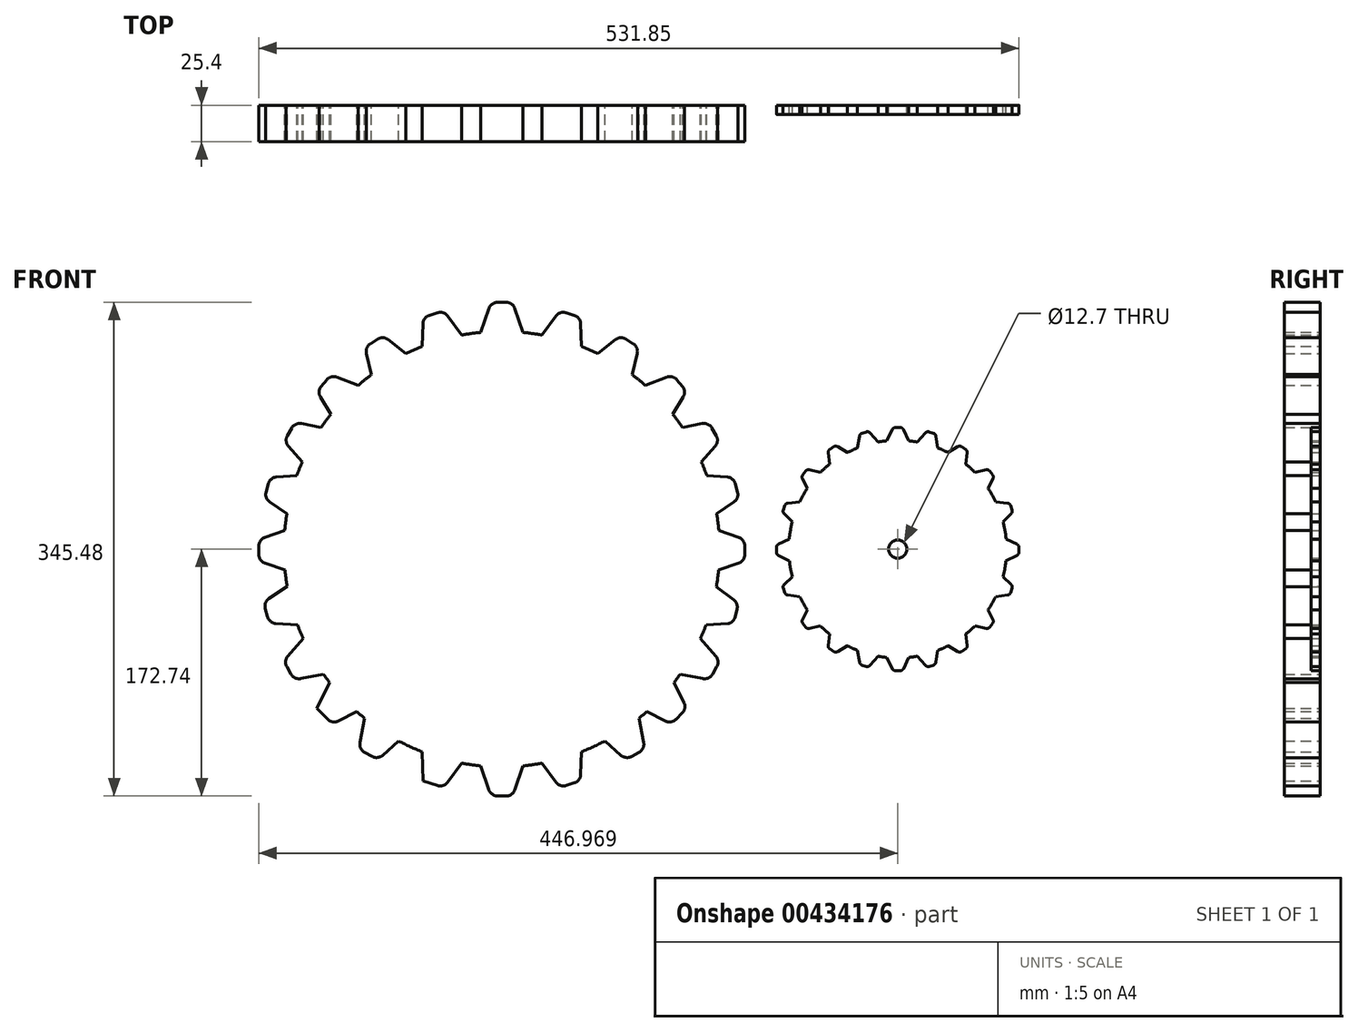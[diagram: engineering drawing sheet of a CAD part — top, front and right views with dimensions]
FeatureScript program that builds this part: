
annotation { "Feature Type Name" : "Feature", "Feature Type Description" : "" }
export const myFeature = defineFeature(function(context is Context, id is Id, definition is map)
    precondition{}
    {
        {
            var Q0;
            Q0=qCreatedBy(makeId("Front.planeOp"),FACE);
            var sketch = newSketch(context, id + "F0", { "sketchPlane" : qUnion([Q0])});
            skCircle(sketch, "E0", {"center": v(0, 0) * mm, "radius": 152.4 * mm});
            skCircle(sketch, "E1", {"center": v(0, 0) * mm, "radius": 6.35 * mm});
            skCircle(sketch, "E2", {"center": v(276.99, 0) * mm, "radius": 76.2 * mm});
            skCircle(sketch, "E3", {"center": v(276.99, 0) * mm, "radius": 6.35 * mm});
            skCircle(sketch, "E4.MirrorC", {"center": v(0, 0) * mm, "radius": 152.34 * mm});
            skLineSegment(sketch, "E5", {"start": v(3.18, 172.74) * mm, "end": v(-2.97, 172.74) * mm});
            skLineSegment(sketch, "E6", {"start": v(-8.98, 168.44) * mm, "end": v(-15.7, 148.7) * mm});
            skLineSegment(sketch, "E7", {"start": v(9.19, 168.44) * mm, "end": v(15.9, 148.7) * mm});
            skLineSegment(sketch, "E8", {"start": v(-15.7, 148.7) * mm, "end": v(15.9, 148.7) * mm});
            skLineSegment(sketch, "E9.MirrorCS", {"start": v(15.9, -148.7) * mm, "end": v(-15.7, -148.7) * mm});
            skLineSegment(sketch, "E10.MirrorCS", {"start": v(-8.98, -168.44) * mm, "end": v(-15.7, -148.7) * mm});
            skLineSegment(sketch, "E11.MirrorCS", {"start": v(9.19, -168.44) * mm, "end": v(15.9, -148.7) * mm});
            skLineSegment(sketch, "E12.MirrorCS", {"start": v(3.18, -172.74) * mm, "end": v(-2.97, -172.74) * mm});
            skLineSegment(sketch, "E13", {"start": v(-44.83, 165.44) * mm, "end": v(-50.7, 163.63) * mm});
            skLineSegment(sketch, "E14", {"start": v(-55.17, 157.74) * mm, "end": v(-55.75, 136.9) * mm});
            skLineSegment(sketch, "E15", {"start": v(-37.81, 163.1) * mm, "end": v(-25.57, 146.23) * mm});
            skLineSegment(sketch, "E16", {"start": v(-25.57, 146.23) * mm, "end": v(-55.75, 136.9) * mm});
            skLineSegment(sketch, "E17.0", {"start": v(-55.75, 136.9) * mm, "end": v(-25.57, 146.23) * mm, "construction": true});
            skLineSegment(sketch, "E18", {"start": v(-86.8, 146.99) * mm, "end": v(-92, 143.69) * mm});
            skLineSegment(sketch, "E19", {"start": v(-94.75, 136.83) * mm, "end": v(-89.8, 116.57) * mm});
            skLineSegment(sketch, "E20", {"start": v(-79.43, 146.59) * mm, "end": v(-63.16, 133.55) * mm});
            skLineSegment(sketch, "E21", {"start": v(-63.16, 133.55) * mm, "end": v(-89.8, 116.57) * mm});
            skLineSegment(sketch, "E22.0", {"start": v(-89.8, 116.57) * mm, "end": v(-63.16, 133.55) * mm, "construction": true});
            skLineSegment(sketch, "E23", {"start": v(-122.43, 118.55) * mm, "end": v(-126.38, 113.84) * mm});
            skLineSegment(sketch, "E24", {"start": v(-126.95, 106.47) * mm, "end": v(-116.14, 88.64) * mm});
            skLineSegment(sketch, "E25", {"start": v(-115.27, 120.39) * mm, "end": v(-95.83, 112.84) * mm});
            skLineSegment(sketch, "E26", {"start": v(-95.83, 112.84) * mm, "end": v(-116.14, 88.64) * mm});
            skLineSegment(sketch, "E27.0", {"start": v(-116.14, 88.64) * mm, "end": v(-95.83, 112.84) * mm, "construction": true});
            skLineSegment(sketch, "E28", {"start": v(-146.98, 84.77) * mm, "end": v(-150.05, 79.45) * mm});
            skLineSegment(sketch, "E29", {"start": v(-149.33, 72.1) * mm, "end": v(-135.58, 56.4) * mm});
            skLineSegment(sketch, "E30", {"start": v(-140.24, 87.83) * mm, "end": v(-119.79, 83.77) * mm});
            skLineSegment(sketch, "E31", {"start": v(-119.79, 83.77) * mm, "end": v(-135.58, 56.4) * mm});
            skLineSegment(sketch, "E32.0", {"start": v(-135.58, 56.4) * mm, "end": v(-119.79, 83.77) * mm, "construction": true});
            skLineSegment(sketch, "E33", {"start": v(-163.39, 45.78) * mm, "end": v(-164.98, 39.84) * mm});
            skLineSegment(sketch, "E34", {"start": v(-162.38, 32.92) * mm, "end": v(-145.04, 21.33) * mm});
            skLineSegment(sketch, "E35", {"start": v(-157.67, 50.47) * mm, "end": v(-136.87, 51.84) * mm});
            skLineSegment(sketch, "E36", {"start": v(-136.87, 51.84) * mm, "end": v(-145.04, 21.33) * mm});
            skLineSegment(sketch, "E37.0", {"start": v(-145.04, 21.33) * mm, "end": v(-136.87, 51.84) * mm, "construction": true});
            skLineSegment(sketch, "E38", {"start": v(-169.98, 2.28) * mm, "end": v(-169.98, -3.87) * mm});
            skLineSegment(sketch, "E39", {"start": v(-165.68, -9.88) * mm, "end": v(-145.94, -16.6) * mm});
            skLineSegment(sketch, "E40", {"start": v(-165.68, 8.29) * mm, "end": v(-145.94, 15) * mm});
            skLineSegment(sketch, "E41", {"start": v(-145.94, 15) * mm, "end": v(-145.94, -16.6) * mm});
            skLineSegment(sketch, "E42", {"start": v(-165.5, -41.42) * mm, "end": v(-163.9, -47.35) * mm});
            skLineSegment(sketch, "E43", {"start": v(-158.2, -52.05) * mm, "end": v(-137.39, -53.42) * mm});
            skLineSegment(sketch, "E44", {"start": v(-162.9, -34.5) * mm, "end": v(-145.56, -22.9) * mm});
            skLineSegment(sketch, "E45", {"start": v(-145.56, -22.9) * mm, "end": v(-137.39, -53.42) * mm});
            skLineSegment(sketch, "E46.0", {"start": v(-137.39, -53.42) * mm, "end": v(-145.56, -22.9) * mm, "construction": true});
            skLineSegment(sketch, "E47", {"start": v(-150.42, -82.21) * mm, "end": v(-147.35, -87.53) * mm});
            skLineSegment(sketch, "E48", {"start": v(-140.62, -90.59) * mm, "end": v(-120.16, -86.53) * mm});
            skLineSegment(sketch, "E49", {"start": v(-149.7, -74.85) * mm, "end": v(-135.96, -59.17) * mm});
            skLineSegment(sketch, "E50", {"start": v(-135.96, -59.17) * mm, "end": v(-120.16, -86.53) * mm});
            skLineSegment(sketch, "E51.0", {"start": v(-120.16, -86.53) * mm, "end": v(-135.96, -59.17) * mm, "construction": true});
            skLineSegment(sketch, "E52", {"start": v(-129.47, -111.53) * mm, "end": v(-121.91, -119.1) * mm});
            skLineSegment(sketch, "E53", {"start": v(-114.62, -120.3) * mm, "end": v(-95.91, -111.09) * mm});
            skLineSegment(sketch, "E54", {"start": v(-129.47, -111.53) * mm, "end": v(-118.25, -88.75) * mm});
            skLineSegment(sketch, "E55", {"start": v(-118.25, -88.75) * mm, "end": v(-95.91, -111.09) * mm});
            skLineSegment(sketch, "E56.0", {"start": v(-95.91, -111.09) * mm, "end": v(-118.25, -88.75) * mm, "construction": true});
            skLineSegment(sketch, "E57", {"start": v(-96.16, -142.05) * mm, "end": v(-90.81, -145.08) * mm});
            skLineSegment(sketch, "E58", {"start": v(-83.46, -144.3) * mm, "end": v(-67.9, -130.42) * mm});
            skLineSegment(sketch, "E59", {"start": v(-99.27, -135.35) * mm, "end": v(-95.39, -114.86) * mm});
            skLineSegment(sketch, "E60", {"start": v(-95.39, -114.86) * mm, "end": v(-67.9, -130.42) * mm});
            skLineSegment(sketch, "E61.0", {"start": v(-67.9, -130.42) * mm, "end": v(-95.39, -114.86) * mm, "construction": true});
            skLineSegment(sketch, "E62.MirrorCS", {"start": v(-37.81, -163.1) * mm, "end": v(-25.57, -146.23) * mm});
            skLineSegment(sketch, "E63.MirrorCS", {"start": v(-55.75, -136.9) * mm, "end": v(-25.57, -146.23) * mm, "construction": true});
            skLineSegment(sketch, "E64.MirrorCS", {"start": v(-55.05, -162.29) * mm, "end": v(-55.75, -136.9) * mm});
            skLineSegment(sketch, "E65.MirrorCS", {"start": v(-44.83, -165.44) * mm, "end": v(-55.05, -162.29) * mm});
            skLineSegment(sketch, "E66.MirrorCS", {"start": v(157.67, 50.47) * mm, "end": v(136.87, 51.84) * mm});
            skLineSegment(sketch, "E67.MirrorCS", {"start": v(162.38, 32.92) * mm, "end": v(145.04, 21.33) * mm});
            skLineSegment(sketch, "E68.MirrorCS", {"start": v(163.39, 45.78) * mm, "end": v(164.98, 39.84) * mm});
            skLineSegment(sketch, "E69.MirrorCS", {"start": v(145.04, 21.33) * mm, "end": v(136.87, 51.84) * mm, "construction": true});
            skLineSegment(sketch, "E70.MirrorCS", {"start": v(145.94, 15) * mm, "end": v(145.94, -16.6) * mm});
            skLineSegment(sketch, "E71.MirrorCS", {"start": v(165.68, 8.29) * mm, "end": v(145.94, 15) * mm});
            skLineSegment(sketch, "E72.MirrorCS", {"start": v(169.98, 2.28) * mm, "end": v(169.98, -3.87) * mm});
            skLineSegment(sketch, "E73.MirrorCS", {"start": v(165.68, -9.88) * mm, "end": v(145.94, -16.6) * mm});
            skLineSegment(sketch, "E74.MirrorCS", {"start": v(137.39, -53.42) * mm, "end": v(145.56, -22.9) * mm, "construction": true});
            skLineSegment(sketch, "E75.MirrorCS", {"start": v(162.27, -35.45) * mm, "end": v(145.56, -22.9) * mm});
            skLineSegment(sketch, "E76.MirrorCS", {"start": v(164.59, -42.17) * mm, "end": v(163, -48.1) * mm});
            skLineSegment(sketch, "E77.MirrorCS", {"start": v(149.7, -74.85) * mm, "end": v(135.96, -59.17) * mm});
            skLineSegment(sketch, "E78.MirrorCS", {"start": v(150.42, -82.21) * mm, "end": v(147.35, -87.53) * mm});
            skLineSegment(sketch, "E79.MirrorCS", {"start": v(140.62, -90.59) * mm, "end": v(120.16, -86.53) * mm});
            skLineSegment(sketch, "E80.MirrorCS", {"start": v(120.16, -86.53) * mm, "end": v(135.96, -59.17) * mm, "construction": true});
            skLineSegment(sketch, "E81.MirrorCS", {"start": v(95.91, -111.09) * mm, "end": v(118.25, -88.75) * mm, "construction": true});
            skLineSegment(sketch, "E82.MirrorCS", {"start": v(114.62, -120.3) * mm, "end": v(95.91, -111.09) * mm});
            skLineSegment(sketch, "E83.MirrorCS", {"start": v(126.26, -114.75) * mm, "end": v(121.91, -119.1) * mm});
            skLineSegment(sketch, "E84.MirrorCS", {"start": v(127.46, -107.45) * mm, "end": v(118.25, -88.75) * mm});
            skLineSegment(sketch, "E85.MirrorCS", {"start": v(99.27, -135.35) * mm, "end": v(95.39, -114.86) * mm});
            skLineSegment(sketch, "E86.MirrorCS", {"start": v(67.9, -130.42) * mm, "end": v(95.39, -114.86) * mm, "construction": true});
            skLineSegment(sketch, "E87.MirrorCS", {"start": v(83.46, -144.3) * mm, "end": v(67.9, -130.42) * mm});
            skLineSegment(sketch, "E88.MirrorCS", {"start": v(96.16, -142.05) * mm, "end": v(90.81, -145.08) * mm});
            skLineSegment(sketch, "E89.MirrorCS", {"start": v(55.17, -157.74) * mm, "end": v(55.75, -136.9) * mm});
            skLineSegment(sketch, "E90.MirrorCS", {"start": v(55.75, -136.9) * mm, "end": v(25.57, -146.23) * mm, "construction": true});
            skLineSegment(sketch, "E91.MirrorCS", {"start": v(44.83, -165.44) * mm, "end": v(50.7, -163.63) * mm});
            skLineSegment(sketch, "E92.MirrorCS", {"start": v(37.81, -163.1) * mm, "end": v(25.57, -146.23) * mm});
            skLineSegment(sketch, "E93.MirrorCS", {"start": v(37.81, 163.1) * mm, "end": v(25.57, 146.23) * mm});
            skLineSegment(sketch, "E94.MirrorCS", {"start": v(55.17, 157.74) * mm, "end": v(55.75, 136.9) * mm});
            skLineSegment(sketch, "E95.MirrorCS", {"start": v(44.83, 165.44) * mm, "end": v(50.7, 163.63) * mm});
            skLineSegment(sketch, "E96.MirrorCS", {"start": v(55.75, 136.9) * mm, "end": v(25.57, 146.23) * mm, "construction": true});
            skLineSegment(sketch, "E97.MirrorCS", {"start": v(89.8, 116.57) * mm, "end": v(63.16, 133.55) * mm, "construction": true});
            skLineSegment(sketch, "E98.MirrorCS", {"start": v(79.43, 146.59) * mm, "end": v(63.16, 133.55) * mm});
            skLineSegment(sketch, "E99.MirrorCS", {"start": v(94.75, 136.83) * mm, "end": v(89.8, 116.57) * mm});
            skLineSegment(sketch, "E100.MirrorCS", {"start": v(86.8, 146.99) * mm, "end": v(92, 143.69) * mm});
            skLineSegment(sketch, "E101.MirrorCS", {"start": v(115.27, 120.39) * mm, "end": v(95.83, 112.84) * mm});
            skLineSegment(sketch, "E102.MirrorCS", {"start": v(122.43, 118.55) * mm, "end": v(126.38, 113.84) * mm});
            skLineSegment(sketch, "E103.MirrorCS", {"start": v(126.95, 106.47) * mm, "end": v(116.14, 88.64) * mm});
            skLineSegment(sketch, "E104.MirrorCS", {"start": v(116.14, 88.64) * mm, "end": v(95.83, 112.84) * mm, "construction": true});
            skLineSegment(sketch, "E105.MirrorCS", {"start": v(140.24, 87.83) * mm, "end": v(119.79, 83.77) * mm});
            skLineSegment(sketch, "E106.MirrorCS", {"start": v(146.98, 84.77) * mm, "end": v(150.05, 79.45) * mm});
            skLineSegment(sketch, "E107.MirrorCS", {"start": v(149.33, 72.1) * mm, "end": v(135.58, 56.4) * mm});
            skLineSegment(sketch, "E108.MirrorCS", {"start": v(135.58, 56.4) * mm, "end": v(119.79, 83.77) * mm, "construction": true});
            skLineSegment(sketch, "E109", {"start": v(193.5, -4.35) * mm, "end": v(203.46, -9.32) * mm});
            skLineSegment(sketch, "E110", {"start": v(192.1, -2.08) * mm, "end": v(192.1, 1.1) * mm});
            skLineSegment(sketch, "E111", {"start": v(193.56, 3.4) * mm, "end": v(203.6, 8.1) * mm});
            skLineSegment(sketch, "E112", {"start": v(203.6, 8.1) * mm, "end": v(203.46, -9.32) * mm});
            skLineSegment(sketch, "E113", {"start": v(250.25, 79.12) * mm, "end": v(248.45, 68.13) * mm});
            skLineSegment(sketch, "E114", {"start": v(252, 81.13) * mm, "end": v(255.03, 82.07) * mm});
            skLineSegment(sketch, "E115", {"start": v(257.66, 81.36) * mm, "end": v(265.14, 73.17) * mm});
            skLineSegment(sketch, "E116", {"start": v(265.14, 73.17) * mm, "end": v(248.45, 68.13) * mm});
            skLineSegment(sketch, "E117", {"start": v(228.41, 67.51) * mm, "end": v(229.64, 56.45) * mm});
            skLineSegment(sketch, "E118", {"start": v(229.56, 69.92) * mm, "end": v(232.22, 71.64) * mm});
            skLineSegment(sketch, "E119", {"start": v(234.94, 71.66) * mm, "end": v(244.35, 65.8) * mm});
            skLineSegment(sketch, "E120", {"start": v(244.35, 65.8) * mm, "end": v(229.64, 56.45) * mm});
            skLineSegment(sketch, "E121", {"start": v(210.32, 49.36) * mm, "end": v(215.2, 39.35) * mm});
            skLineSegment(sketch, "E122", {"start": v(210.59, 52.02) * mm, "end": v(212.51, 54.53) * mm});
            skLineSegment(sketch, "E123", {"start": v(215.07, 55.47) * mm, "end": v(225.9, 53.11) * mm});
            skLineSegment(sketch, "E124", {"start": v(225.9, 53.11) * mm, "end": v(215.2, 39.35) * mm});
            skLineSegment(sketch, "E125", {"start": v(197.57, 24.8) * mm, "end": v(205.5, 17) * mm});
            skLineSegment(sketch, "E126", {"start": v(196.94, 27.39) * mm, "end": v(197.91, 30.4) * mm});
            skLineSegment(sketch, "E127", {"start": v(200.01, 32.14) * mm, "end": v(211.01, 33.53) * mm});
            skLineSegment(sketch, "E128", {"start": v(211.01, 33.53) * mm, "end": v(205.5, 17) * mm});
            skLineSegment(sketch, "E129.MirrorCS", {"start": v(197.57, -24.8) * mm, "end": v(205.5, -17) * mm});
            skLineSegment(sketch, "E130.MirrorCS", {"start": v(211.01, -33.53) * mm, "end": v(205.5, -17) * mm});
            skLineSegment(sketch, "E131.MirrorCS", {"start": v(200.01, -32.14) * mm, "end": v(211.01, -33.53) * mm});
            skLineSegment(sketch, "E132.MirrorCS", {"start": v(196.94, -27.39) * mm, "end": v(197.91, -30.4) * mm});
            skLineSegment(sketch, "E133.MirrorCS", {"start": v(210.32, -49.36) * mm, "end": v(215.2, -39.35) * mm});
            skLineSegment(sketch, "E134.MirrorCS", {"start": v(225.9, -53.11) * mm, "end": v(215.2, -39.35) * mm});
            skLineSegment(sketch, "E135.MirrorCS", {"start": v(215.07, -55.47) * mm, "end": v(225.9, -53.11) * mm});
            skLineSegment(sketch, "E136.MirrorCS", {"start": v(210.59, -52.02) * mm, "end": v(212.51, -54.53) * mm});
            skLineSegment(sketch, "E137.MirrorCS", {"start": v(229.56, -69.92) * mm, "end": v(232.22, -71.64) * mm});
            skLineSegment(sketch, "E138.MirrorCS", {"start": v(228.41, -67.51) * mm, "end": v(229.64, -56.45) * mm});
            skLineSegment(sketch, "E139.MirrorCS", {"start": v(234.94, -71.66) * mm, "end": v(244.35, -65.8) * mm});
            skLineSegment(sketch, "E140.MirrorCS", {"start": v(244.35, -65.8) * mm, "end": v(229.64, -56.45) * mm});
            skLineSegment(sketch, "E141.MirrorCS", {"start": v(265.14, -73.17) * mm, "end": v(248.45, -68.13) * mm});
            skLineSegment(sketch, "E142.MirrorCS", {"start": v(250.25, -79.12) * mm, "end": v(248.45, -68.13) * mm});
            skLineSegment(sketch, "E143.MirrorCS", {"start": v(252, -81.13) * mm, "end": v(255.03, -82.07) * mm});
            skLineSegment(sketch, "E144.MirrorCS", {"start": v(257.66, -81.36) * mm, "end": v(265.14, -73.17) * mm});
            skLineSegment(sketch, "E145.MirrorCS", {"start": v(296.32, 81.36) * mm, "end": v(288.84, 73.17) * mm});
            skLineSegment(sketch, "E146.MirrorCS", {"start": v(288.84, 73.17) * mm, "end": v(305.53, 68.13) * mm});
            skLineSegment(sketch, "E147.MirrorCS", {"start": v(303.73, 79.12) * mm, "end": v(305.53, 68.13) * mm});
            skLineSegment(sketch, "E148.MirrorCS", {"start": v(301.97, 81.13) * mm, "end": v(298.95, 82.07) * mm});
            skLineSegment(sketch, "E149.MirrorCS", {"start": v(324.42, 69.92) * mm, "end": v(321.76, 71.64) * mm});
            skLineSegment(sketch, "E150.MirrorCS", {"start": v(319.04, 71.66) * mm, "end": v(309.63, 65.8) * mm});
            skLineSegment(sketch, "E151.MirrorCS", {"start": v(325.57, 67.51) * mm, "end": v(324.34, 56.45) * mm});
            skLineSegment(sketch, "E152.MirrorCS", {"start": v(309.63, 65.8) * mm, "end": v(324.34, 56.45) * mm});
            skLineSegment(sketch, "E153.MirrorCS", {"start": v(328.07, 53.11) * mm, "end": v(338.78, 39.35) * mm});
            skLineSegment(sketch, "E154.MirrorCS", {"start": v(338.9, 55.47) * mm, "end": v(328.07, 53.11) * mm});
            skLineSegment(sketch, "E155.MirrorCS", {"start": v(343.39, 52.02) * mm, "end": v(341.46, 54.53) * mm});
            skLineSegment(sketch, "E156.MirrorCS", {"start": v(343.66, 49.36) * mm, "end": v(338.78, 39.35) * mm});
            skLineSegment(sketch, "E157.MirrorCS", {"start": v(353.97, 32.14) * mm, "end": v(342.97, 33.53) * mm});
            skLineSegment(sketch, "E158.MirrorCS", {"start": v(342.97, 33.53) * mm, "end": v(348.47, 17) * mm});
            skLineSegment(sketch, "E159.MirrorCS", {"start": v(356.4, 24.8) * mm, "end": v(348.47, 17) * mm});
            skLineSegment(sketch, "E160.MirrorCS", {"start": v(357.04, 27.39) * mm, "end": v(356.06, 30.4) * mm});
            skLineSegment(sketch, "E161.MirrorCS", {"start": v(350.38, 8.1) * mm, "end": v(350.51, -9.32) * mm});
            skLineSegment(sketch, "E162.MirrorCS", {"start": v(360.41, 3.4) * mm, "end": v(350.38, 8.1) * mm});
            skLineSegment(sketch, "E163.MirrorCS", {"start": v(361.87, -2.08) * mm, "end": v(361.87, 1.1) * mm});
            skLineSegment(sketch, "E164.MirrorCS", {"start": v(360.47, -4.35) * mm, "end": v(350.51, -9.32) * mm});
            skLineSegment(sketch, "E165.MirrorCS", {"start": v(356.4, -24.8) * mm, "end": v(348.47, -17) * mm});
            skLineSegment(sketch, "E166.MirrorCS", {"start": v(357.04, -27.39) * mm, "end": v(356.06, -30.4) * mm});
            skLineSegment(sketch, "E167.MirrorCS", {"start": v(353.97, -32.14) * mm, "end": v(342.97, -33.53) * mm});
            skLineSegment(sketch, "E168.MirrorCS", {"start": v(342.97, -33.53) * mm, "end": v(348.47, -17) * mm});
            skLineSegment(sketch, "E169.MirrorCS", {"start": v(328.07, -53.11) * mm, "end": v(338.78, -39.35) * mm});
            skLineSegment(sketch, "E170.MirrorCS", {"start": v(343.66, -49.36) * mm, "end": v(338.78, -39.35) * mm});
            skLineSegment(sketch, "E171.MirrorCS", {"start": v(343.39, -52.02) * mm, "end": v(341.46, -54.53) * mm});
            skLineSegment(sketch, "E172.MirrorCS", {"start": v(338.9, -55.47) * mm, "end": v(328.07, -53.11) * mm});
            skLineSegment(sketch, "E173.MirrorCS", {"start": v(325.57, -67.51) * mm, "end": v(324.34, -56.45) * mm});
            skLineSegment(sketch, "E174.MirrorCS", {"start": v(309.63, -65.8) * mm, "end": v(324.34, -56.45) * mm});
            skLineSegment(sketch, "E175.MirrorCS", {"start": v(319.04, -71.66) * mm, "end": v(309.63, -65.8) * mm});
            skLineSegment(sketch, "E176.MirrorCS", {"start": v(324.42, -69.92) * mm, "end": v(321.76, -71.64) * mm});
            skLineSegment(sketch, "E177.MirrorCS", {"start": v(288.84, -73.17) * mm, "end": v(305.53, -68.13) * mm});
            skLineSegment(sketch, "E178.MirrorCS", {"start": v(303.73, -79.12) * mm, "end": v(305.53, -68.13) * mm});
            skLineSegment(sketch, "E179.MirrorCS", {"start": v(301.97, -81.13) * mm, "end": v(298.95, -82.07) * mm});
            skLineSegment(sketch, "E180.MirrorCS", {"start": v(296.32, -81.36) * mm, "end": v(288.84, -73.17) * mm});
            skLineSegment(sketch, "E181", {"start": v(273.24, 83.72) * mm, "end": v(268.26, 73.77) * mm});
            skLineSegment(sketch, "E182", {"start": v(275.51, 85.12) * mm, "end": v(278.68, 85.12) * mm});
            skLineSegment(sketch, "E183", {"start": v(280.98, 83.67) * mm, "end": v(285.7, 73.63) * mm});
            skLineSegment(sketch, "E184", {"start": v(285.7, 73.63) * mm, "end": v(268.26, 73.77) * mm});
            skLineSegment(sketch, "E185.MirrorCS", {"start": v(285.7, -73.63) * mm, "end": v(268.26, -73.77) * mm});
            skLineSegment(sketch, "E186.MirrorCS", {"start": v(280.98, -83.67) * mm, "end": v(285.7, -73.63) * mm});
            skLineSegment(sketch, "E187.MirrorCS", {"start": v(273.24, -83.72) * mm, "end": v(268.26, -73.77) * mm});
            skLineSegment(sketch, "E188.MirrorCS", {"start": v(275.51, -85.12) * mm, "end": v(278.68, -85.12) * mm});
            skPoint(sketch, "E189.visualSharp", {"position": v(-55.05, 162.29) * mm});
            skArc(sketch, "E189.filletArc", {"start": v(-50.7, 163.63) * mm, "mid": v(-53.88, 161.4) * mm, "end": v(-55.17, 157.74) * mm});
            skPoint(sketch, "E190.visualSharp", {"position": v(-40.49, 166.79) * mm});
            skArc(sketch, "E190.filletArc", {"start": v(-37.81, 163.1) * mm, "mid": v(-40.95, 165.4) * mm, "end": v(-44.83, 165.44) * mm});
            skPoint(sketch, "E191.visualSharp", {"position": v(-7.51, 172.74) * mm});
            skArc(sketch, "E191.filletArc", {"start": v(-2.97, 172.74) * mm, "mid": v(-6.66, 171.56) * mm, "end": v(-8.98, 168.44) * mm});
            skPoint(sketch, "E192.visualSharp", {"position": v(7.73, 172.74) * mm});
            skArc(sketch, "E192.filletArc", {"start": v(9.19, 168.44) * mm, "mid": v(6.88, 171.56) * mm, "end": v(3.18, 172.74) * mm});
            skPoint(sketch, "E193.visualSharp", {"position": v(40.49, 166.79) * mm});
            skArc(sketch, "E193.filletArc", {"start": v(44.83, 165.44) * mm, "mid": v(40.95, 165.4) * mm, "end": v(37.81, 163.1) * mm});
            skPoint(sketch, "E194.visualSharp", {"position": v(55.05, 162.29) * mm});
            skArc(sketch, "E194.filletArc", {"start": v(55.17, 157.74) * mm, "mid": v(53.88, 161.4) * mm, "end": v(50.7, 163.63) * mm});
            skPoint(sketch, "E195.visualSharp", {"position": v(82.97, 149.43) * mm});
            skArc(sketch, "E195.filletArc", {"start": v(86.8, 146.99) * mm, "mid": v(83.05, 147.98) * mm, "end": v(79.43, 146.59) * mm});
            skPoint(sketch, "E196.visualSharp", {"position": v(95.83, 141.24) * mm});
            skArc(sketch, "E196.filletArc", {"start": v(94.75, 136.83) * mm, "mid": v(94.47, 140.7) * mm, "end": v(92, 143.69) * mm});
            skPoint(sketch, "E197.visualSharp", {"position": v(119.5, 122.03) * mm});
            skArc(sketch, "E197.filletArc", {"start": v(122.43, 118.55) * mm, "mid": v(119.14, 120.62) * mm, "end": v(115.27, 120.39) * mm});
            skPoint(sketch, "E198.visualSharp", {"position": v(129.3, 110.36) * mm});
            skArc(sketch, "E198.filletArc", {"start": v(126.95, 106.47) * mm, "mid": v(127.85, 110.25) * mm, "end": v(126.38, 113.84) * mm});
            skPoint(sketch, "E199.visualSharp", {"position": v(144.7, 88.71) * mm});
            skArc(sketch, "E199.filletArc", {"start": v(146.98, 84.77) * mm, "mid": v(144.1, 87.38) * mm, "end": v(140.24, 87.83) * mm});
            skPoint(sketch, "E200.visualSharp", {"position": v(162.21, 50.17) * mm});
            skArc(sketch, "E200.filletArc", {"start": v(163.39, 45.78) * mm, "mid": v(161.29, 49.04) * mm, "end": v(157.67, 50.47) * mm});
            skPoint(sketch, "E201.visualSharp", {"position": v(166.16, 35.45) * mm});
            skArc(sketch, "E201.filletArc", {"start": v(162.38, 32.92) * mm, "mid": v(164.79, 35.96) * mm, "end": v(164.98, 39.84) * mm});
            skPoint(sketch, "E202.visualSharp", {"position": v(169.98, 6.82) * mm});
            skArc(sketch, "E202.filletArc", {"start": v(169.98, 2.28) * mm, "mid": v(168.8, 5.97) * mm, "end": v(165.68, 8.29) * mm});
            skPoint(sketch, "E203.visualSharp", {"position": v(169.98, -8.42) * mm});
            skArc(sketch, "E203.filletArc", {"start": v(165.68, -9.88) * mm, "mid": v(168.8, -7.57) * mm, "end": v(169.98, -3.87) * mm});
            skPoint(sketch, "E204.visualSharp", {"position": v(165.7, -38.03) * mm});
            skArc(sketch, "E204.filletArc", {"start": v(164.59, -42.17) * mm, "mid": v(164.45, -38.46) * mm, "end": v(162.27, -35.45) * mm});
            skPoint(sketch, "E205.visualSharp", {"position": v(152.7, -78.28) * mm});
            skArc(sketch, "E205.filletArc", {"start": v(150.42, -82.21) * mm, "mid": v(151.24, -78.42) * mm, "end": v(149.7, -74.85) * mm});
            skPoint(sketch, "E206.visualSharp", {"position": v(145.08, -91.47) * mm});
            skArc(sketch, "E206.filletArc", {"start": v(140.62, -90.59) * mm, "mid": v(144.47, -90.14) * mm, "end": v(147.35, -87.53) * mm});
            skPoint(sketch, "E207.visualSharp", {"position": v(129.47, -111.53) * mm});
            skArc(sketch, "E207.filletArc", {"start": v(126.26, -114.75) * mm, "mid": v(128.03, -111.3) * mm, "end": v(127.46, -107.45) * mm});
            skPoint(sketch, "E208.visualSharp", {"position": v(118.7, -122.3) * mm});
            skArc(sketch, "E208.filletArc", {"start": v(114.62, -120.3) * mm, "mid": v(118.46, -120.87) * mm, "end": v(121.91, -119.1) * mm});
            skPoint(sketch, "E209.visualSharp", {"position": v(100.12, -139.81) * mm});
            skArc(sketch, "E209.filletArc", {"start": v(96.16, -142.05) * mm, "mid": v(98.8, -139.2) * mm, "end": v(99.27, -135.35) * mm});
            skPoint(sketch, "E210.visualSharp", {"position": v(86.85, -147.32) * mm});
            skArc(sketch, "E210.filletArc", {"start": v(83.46, -144.3) * mm, "mid": v(87, -145.87) * mm, "end": v(90.81, -145.08) * mm});
            skPoint(sketch, "E211.visualSharp", {"position": v(55.05, -162.29) * mm});
            skArc(sketch, "E211.filletArc", {"start": v(50.7, -163.63) * mm, "mid": v(53.88, -161.4) * mm, "end": v(55.17, -157.74) * mm});
            skPoint(sketch, "E212.visualSharp", {"position": v(7.73, -172.74) * mm});
            skArc(sketch, "E212.filletArc", {"start": v(3.18, -172.74) * mm, "mid": v(6.88, -171.56) * mm, "end": v(9.19, -168.44) * mm});
            skPoint(sketch, "E213.visualSharp", {"position": v(40.49, -166.79) * mm});
            skArc(sketch, "E213.filletArc", {"start": v(37.81, -163.1) * mm, "mid": v(40.95, -165.4) * mm, "end": v(44.83, -165.44) * mm});
            skPoint(sketch, "E214.visualSharp", {"position": v(-7.51, -172.74) * mm});
            skArc(sketch, "E214.filletArc", {"start": v(-8.98, -168.44) * mm, "mid": v(-6.66, -171.56) * mm, "end": v(-2.97, -172.74) * mm});
            skPoint(sketch, "E215.visualSharp", {"position": v(-40.49, -166.79) * mm});
            skArc(sketch, "E215.filletArc", {"start": v(-44.83, -165.44) * mm, "mid": v(-40.95, -165.4) * mm, "end": v(-37.81, -163.1) * mm});
            skPoint(sketch, "E216.visualSharp", {"position": v(-86.85, -147.32) * mm});
            skArc(sketch, "E216.filletArc", {"start": v(-90.81, -145.08) * mm, "mid": v(-87, -145.87) * mm, "end": v(-83.46, -144.3) * mm});
            skPoint(sketch, "E217.visualSharp", {"position": v(-100.12, -139.81) * mm});
            skArc(sketch, "E217.filletArc", {"start": v(-99.27, -135.35) * mm, "mid": v(-98.8, -139.2) * mm, "end": v(-96.16, -142.05) * mm});
            skPoint(sketch, "E218.visualSharp", {"position": v(-118.7, -122.3) * mm});
            skArc(sketch, "E218.filletArc", {"start": v(-121.91, -119.1) * mm, "mid": v(-118.46, -120.87) * mm, "end": v(-114.62, -120.3) * mm});
            skPoint(sketch, "E219.visualSharp", {"position": v(-145.08, -91.47) * mm});
            skArc(sketch, "E219.filletArc", {"start": v(-147.35, -87.53) * mm, "mid": v(-144.47, -90.14) * mm, "end": v(-140.62, -90.59) * mm});
            skPoint(sketch, "E220.visualSharp", {"position": v(-152.7, -78.28) * mm});
            skArc(sketch, "E220.filletArc", {"start": v(-149.7, -74.85) * mm, "mid": v(-151.24, -78.42) * mm, "end": v(-150.42, -82.21) * mm});
            skPoint(sketch, "E221.visualSharp", {"position": v(-162.73, -51.75) * mm});
            skArc(sketch, "E221.filletArc", {"start": v(-163.9, -47.35) * mm, "mid": v(-161.8, -50.62) * mm, "end": v(-158.2, -52.05) * mm});
            skPoint(sketch, "E222.visualSharp", {"position": v(-166.68, -37.03) * mm});
            skArc(sketch, "E222.filletArc", {"start": v(-162.9, -34.5) * mm, "mid": v(-165.31, -37.54) * mm, "end": v(-165.5, -41.42) * mm});
            skPoint(sketch, "E223.visualSharp", {"position": v(-169.98, -8.42) * mm});
            skArc(sketch, "E223.filletArc", {"start": v(-169.98, -3.87) * mm, "mid": v(-168.8, -7.57) * mm, "end": v(-165.68, -9.88) * mm});
            skPoint(sketch, "E224.visualSharp", {"position": v(-169.98, 6.82) * mm});
            skArc(sketch, "E224.filletArc", {"start": v(-165.68, 8.29) * mm, "mid": v(-168.8, 5.97) * mm, "end": v(-169.98, 2.28) * mm});
            skPoint(sketch, "E225.visualSharp", {"position": v(-166.16, 35.45) * mm});
            skArc(sketch, "E225.filletArc", {"start": v(-164.98, 39.84) * mm, "mid": v(-164.79, 35.96) * mm, "end": v(-162.38, 32.92) * mm});
            skPoint(sketch, "E226.visualSharp", {"position": v(-162.21, 50.17) * mm});
            skArc(sketch, "E226.filletArc", {"start": v(-157.67, 50.47) * mm, "mid": v(-161.29, 49.04) * mm, "end": v(-163.39, 45.78) * mm});
            skPoint(sketch, "E227.visualSharp", {"position": v(-152.32, 75.51) * mm});
            skArc(sketch, "E227.filletArc", {"start": v(-150.05, 79.45) * mm, "mid": v(-150.87, 75.66) * mm, "end": v(-149.33, 72.1) * mm});
            skPoint(sketch, "E228.visualSharp", {"position": v(-144.7, 88.71) * mm});
            skArc(sketch, "E228.filletArc", {"start": v(-140.24, 87.83) * mm, "mid": v(-144.1, 87.38) * mm, "end": v(-146.98, 84.77) * mm});
            skPoint(sketch, "E229.visualSharp", {"position": v(-129.3, 110.36) * mm});
            skArc(sketch, "E229.filletArc", {"start": v(-126.38, 113.84) * mm, "mid": v(-127.85, 110.25) * mm, "end": v(-126.95, 106.47) * mm});
            skPoint(sketch, "E230.visualSharp", {"position": v(-119.5, 122.03) * mm});
            skArc(sketch, "E230.filletArc", {"start": v(-115.27, 120.39) * mm, "mid": v(-119.14, 120.62) * mm, "end": v(-122.43, 118.55) * mm});
            skPoint(sketch, "E231.visualSharp", {"position": v(-95.83, 141.24) * mm});
            skArc(sketch, "E231.filletArc", {"start": v(-92, 143.69) * mm, "mid": v(-94.47, 140.7) * mm, "end": v(-94.75, 136.83) * mm});
            skPoint(sketch, "E232.visualSharp", {"position": v(-82.97, 149.43) * mm});
            skArc(sketch, "E232.filletArc", {"start": v(-79.43, 146.59) * mm, "mid": v(-83.05, 147.98) * mm, "end": v(-86.8, 146.99) * mm});
            skPoint(sketch, "E233.visualSharp", {"position": v(152.32, 75.51) * mm});
            skArc(sketch, "E233.filletArc", {"start": v(149.33, 72.1) * mm, "mid": v(150.87, 75.66) * mm, "end": v(150.05, 79.45) * mm});
            skPoint(sketch, "E234.visualSharp", {"position": v(196.45, -25.9) * mm});
            skArc(sketch, "E234.filletArc", {"start": v(197.57, -24.8) * mm, "mid": v(196.89, -26) * mm, "end": v(196.94, -27.39) * mm});
            skPoint(sketch, "E235.visualSharp", {"position": v(198.41, -31.94) * mm});
            skArc(sketch, "E235.filletArc", {"start": v(197.91, -30.4) * mm, "mid": v(198.71, -31.58) * mm, "end": v(200.01, -32.14) * mm});
            skPoint(sketch, "E236.visualSharp", {"position": v(209.63, -50.77) * mm});
            skArc(sketch, "E236.filletArc", {"start": v(210.32, -49.36) * mm, "mid": v(210.08, -50.73) * mm, "end": v(210.59, -52.02) * mm});
            skPoint(sketch, "E237.visualSharp", {"position": v(213.5, -55.81) * mm});
            skArc(sketch, "E237.filletArc", {"start": v(212.51, -54.53) * mm, "mid": v(213.66, -55.37) * mm, "end": v(215.07, -55.47) * mm});
            skPoint(sketch, "E238.visualSharp", {"position": v(228.24, -69.07) * mm});
            skArc(sketch, "E238.filletArc", {"start": v(228.41, -67.51) * mm, "mid": v(228.64, -68.88) * mm, "end": v(229.56, -69.92) * mm});
            skPoint(sketch, "E239.visualSharp", {"position": v(233.57, -72.52) * mm});
            skArc(sketch, "E239.filletArc", {"start": v(232.22, -71.64) * mm, "mid": v(233.58, -72.05) * mm, "end": v(234.94, -71.66) * mm});
            skPoint(sketch, "E240.visualSharp", {"position": v(250.5, -80.66) * mm});
            skArc(sketch, "E240.filletArc", {"start": v(250.25, -79.12) * mm, "mid": v(250.84, -80.37) * mm, "end": v(252, -81.13) * mm});
            skPoint(sketch, "E241.visualSharp", {"position": v(256.57, -82.55) * mm});
            skArc(sketch, "E241.filletArc", {"start": v(255.03, -82.07) * mm, "mid": v(256.45, -82.1) * mm, "end": v(257.66, -81.36) * mm});
            skPoint(sketch, "E242.visualSharp", {"position": v(273.94, -85.12) * mm});
            skArc(sketch, "E242.filletArc", {"start": v(273.24, -83.72) * mm, "mid": v(274.18, -84.75) * mm, "end": v(275.51, -85.12) * mm});
            skPoint(sketch, "E243.visualSharp", {"position": v(280.3, -85.12) * mm});
            skArc(sketch, "E243.filletArc", {"start": v(278.68, -85.12) * mm, "mid": v(280.04, -84.73) * mm, "end": v(280.98, -83.67) * mm});
            skPoint(sketch, "E244.visualSharp", {"position": v(297.4, -82.55) * mm});
            skArc(sketch, "E244.filletArc", {"start": v(296.32, -81.36) * mm, "mid": v(297.53, -82.1) * mm, "end": v(298.95, -82.07) * mm});
            skPoint(sketch, "E245.visualSharp", {"position": v(303.47, -80.66) * mm});
            skArc(sketch, "E245.filletArc", {"start": v(301.97, -81.13) * mm, "mid": v(303.14, -80.37) * mm, "end": v(303.73, -79.12) * mm});
            skPoint(sketch, "E246.visualSharp", {"position": v(320.4, -72.52) * mm});
            skArc(sketch, "E246.filletArc", {"start": v(319.04, -71.66) * mm, "mid": v(320.4, -72.05) * mm, "end": v(321.76, -71.64) * mm});
            skPoint(sketch, "E247.visualSharp", {"position": v(325.74, -69.07) * mm});
            skArc(sketch, "E247.filletArc", {"start": v(324.42, -69.92) * mm, "mid": v(325.33, -68.88) * mm, "end": v(325.57, -67.51) * mm});
            skPoint(sketch, "E248.visualSharp", {"position": v(344.34, -50.77) * mm});
            skArc(sketch, "E248.filletArc", {"start": v(343.39, -52.02) * mm, "mid": v(343.9, -50.73) * mm, "end": v(343.66, -49.36) * mm});
            skPoint(sketch, "E249.visualSharp", {"position": v(340.48, -55.81) * mm});
            skArc(sketch, "E249.filletArc", {"start": v(338.9, -55.47) * mm, "mid": v(340.32, -55.37) * mm, "end": v(341.46, -54.53) * mm});
            skPoint(sketch, "E250.visualSharp", {"position": v(355.57, -31.94) * mm});
            skArc(sketch, "E250.filletArc", {"start": v(353.97, -32.14) * mm, "mid": v(355.27, -31.58) * mm, "end": v(356.06, -30.4) * mm});
            skPoint(sketch, "E251.visualSharp", {"position": v(357.52, -25.9) * mm});
            skArc(sketch, "E251.filletArc", {"start": v(357.04, -27.39) * mm, "mid": v(357.1, -26) * mm, "end": v(356.4, -24.8) * mm});
            skPoint(sketch, "E252.visualSharp", {"position": v(361.87, -3.64) * mm});
            skArc(sketch, "E252.filletArc", {"start": v(360.47, -4.35) * mm, "mid": v(361.5, -3.41) * mm, "end": v(361.87, -2.08) * mm});
            skPoint(sketch, "E253.visualSharp", {"position": v(361.87, 2.7) * mm});
            skArc(sketch, "E253.filletArc", {"start": v(361.87, 1.1) * mm, "mid": v(361.48, 2.45) * mm, "end": v(360.41, 3.4) * mm});
            skPoint(sketch, "E254.visualSharp", {"position": v(357.52, 25.9) * mm});
            skArc(sketch, "E254.filletArc", {"start": v(356.4, 24.8) * mm, "mid": v(357.1, 26) * mm, "end": v(357.04, 27.39) * mm});
            skPoint(sketch, "E255.visualSharp", {"position": v(355.57, 31.94) * mm});
            skArc(sketch, "E255.filletArc", {"start": v(356.06, 30.4) * mm, "mid": v(355.27, 31.58) * mm, "end": v(353.97, 32.14) * mm});
            skPoint(sketch, "E256.visualSharp", {"position": v(340.48, 55.81) * mm});
            skArc(sketch, "E256.filletArc", {"start": v(341.46, 54.53) * mm, "mid": v(340.32, 55.37) * mm, "end": v(338.9, 55.47) * mm});
            skPoint(sketch, "E257.visualSharp", {"position": v(344.34, 50.77) * mm});
            skArc(sketch, "E257.filletArc", {"start": v(343.66, 49.36) * mm, "mid": v(343.9, 50.73) * mm, "end": v(343.39, 52.02) * mm});
            skPoint(sketch, "E258.visualSharp", {"position": v(320.4, 72.52) * mm});
            skArc(sketch, "E258.filletArc", {"start": v(321.76, 71.64) * mm, "mid": v(320.4, 72.05) * mm, "end": v(319.04, 71.66) * mm});
            skPoint(sketch, "E259.visualSharp", {"position": v(325.74, 69.07) * mm});
            skArc(sketch, "E259.filletArc", {"start": v(325.57, 67.51) * mm, "mid": v(325.33, 68.88) * mm, "end": v(324.42, 69.92) * mm});
            skPoint(sketch, "E260.visualSharp", {"position": v(303.47, 80.66) * mm});
            skArc(sketch, "E260.filletArc", {"start": v(303.73, 79.12) * mm, "mid": v(303.14, 80.37) * mm, "end": v(301.97, 81.13) * mm});
            skPoint(sketch, "E261.visualSharp", {"position": v(297.4, 82.55) * mm});
            skArc(sketch, "E261.filletArc", {"start": v(298.95, 82.07) * mm, "mid": v(297.53, 82.1) * mm, "end": v(296.32, 81.36) * mm});
            skPoint(sketch, "E262.visualSharp", {"position": v(273.94, 85.12) * mm});
            skArc(sketch, "E262.filletArc", {"start": v(275.51, 85.12) * mm, "mid": v(274.18, 84.75) * mm, "end": v(273.24, 83.72) * mm});
            skPoint(sketch, "E263.visualSharp", {"position": v(280.3, 85.12) * mm});
            skArc(sketch, "E263.filletArc", {"start": v(280.98, 83.67) * mm, "mid": v(280.04, 84.73) * mm, "end": v(278.68, 85.12) * mm});
            skPoint(sketch, "E264.visualSharp", {"position": v(256.57, 82.55) * mm});
            skArc(sketch, "E264.filletArc", {"start": v(257.66, 81.36) * mm, "mid": v(256.45, 82.1) * mm, "end": v(255.03, 82.07) * mm});
            skPoint(sketch, "E265.visualSharp", {"position": v(233.57, 72.52) * mm});
            skArc(sketch, "E265.filletArc", {"start": v(234.94, 71.66) * mm, "mid": v(233.58, 72.05) * mm, "end": v(232.22, 71.64) * mm});
            skPoint(sketch, "E266.visualSharp", {"position": v(250.5, 80.66) * mm});
            skArc(sketch, "E266.filletArc", {"start": v(252, 81.13) * mm, "mid": v(250.84, 80.37) * mm, "end": v(250.25, 79.12) * mm});
            skPoint(sketch, "E267.visualSharp", {"position": v(228.24, 69.07) * mm});
            skArc(sketch, "E267.filletArc", {"start": v(229.56, 69.92) * mm, "mid": v(228.64, 68.88) * mm, "end": v(228.41, 67.51) * mm});
            skPoint(sketch, "E268.visualSharp", {"position": v(213.5, 55.81) * mm});
            skArc(sketch, "E268.filletArc", {"start": v(215.07, 55.47) * mm, "mid": v(213.66, 55.37) * mm, "end": v(212.51, 54.53) * mm});
            skPoint(sketch, "E269.visualSharp", {"position": v(209.63, 50.77) * mm});
            skArc(sketch, "E269.filletArc", {"start": v(210.59, 52.02) * mm, "mid": v(210.08, 50.73) * mm, "end": v(210.32, 49.36) * mm});
            skPoint(sketch, "E270.visualSharp", {"position": v(198.41, 31.94) * mm});
            skArc(sketch, "E270.filletArc", {"start": v(200.01, 32.14) * mm, "mid": v(198.71, 31.58) * mm, "end": v(197.91, 30.4) * mm});
            skPoint(sketch, "E271.visualSharp", {"position": v(196.45, 25.9) * mm});
            skArc(sketch, "E271.filletArc", {"start": v(196.94, 27.39) * mm, "mid": v(196.89, 26) * mm, "end": v(197.57, 24.8) * mm});
            skPoint(sketch, "E272.visualSharp", {"position": v(192.1, 2.7) * mm});
            skArc(sketch, "E272.filletArc", {"start": v(193.56, 3.4) * mm, "mid": v(192.5, 2.45) * mm, "end": v(192.1, 1.1) * mm});
            skPoint(sketch, "E273.visualSharp", {"position": v(192.1, -3.64) * mm});
            skArc(sketch, "E273.filletArc", {"start": v(192.1, -2.08) * mm, "mid": v(192.48, -3.41) * mm, "end": v(193.5, -4.35) * mm});
            skLineSegment(sketch, "E274", {"start": v(137.39, -53.42) * mm, "end": v(158.2, -52.05) * mm});
            skPoint(sketch, "E275.visualSharp", {"position": v(162, -51.8) * mm});
            skArc(sketch, "E275.filletArc", {"start": v(158.2, -52.05) * mm, "mid": v(161.23, -50.85) * mm, "end": v(163, -48.1) * mm});
            skSolve(sketch);
        }
        {
            var Q0;
            {var subQ5=sQuery(id+"F0.wireOp",EDGE,"E182");Q0=makeQuery(id+"F0.imprint","IMPRINT",FACE,{"disambiguationData":[TD([[makeQuery(id+"F0.imprint","IMPRINT",EDGE,{"derivedFrom":subQ5}),-1.0]])]});}
            var Q1;
            {var subQ5=sQuery(id+"F0.wireOp",EDGE,"E114");Q1=makeQuery(id+"F0.imprint","IMPRINT",FACE,{"disambiguationData":[TD([[makeQuery(id+"F0.imprint","IMPRINT",EDGE,{"derivedFrom":subQ5}),-1.0]])]});}
            var Q2;
            {var subQ5=sQuery(id+"F0.wireOp",EDGE,"E146.MirrorCS");Q2=makeQuery(id+"F0.imprint","IMPRINT",FACE,{"disambiguationData":[TD([[makeQuery(id+"F0.imprint","IMPRINT",EDGE,{"derivedFrom":subQ5}),1.0]])]});}
            var Q3;
            {var subQ5=sQuery(id+"F0.wireOp",EDGE,"E118");Q3=makeQuery(id+"F0.imprint","IMPRINT",FACE,{"disambiguationData":[TD([[makeQuery(id+"F0.imprint","IMPRINT",EDGE,{"derivedFrom":subQ5}),-1.0]])]});}
            var Q4;
            {var subQ5=sQuery(id+"F0.wireOp",EDGE,"E124");Q4=makeQuery(id+"F0.imprint","IMPRINT",FACE,{"disambiguationData":[TD([[makeQuery(id+"F0.imprint","IMPRINT",EDGE,{"derivedFrom":subQ5}),-1.0]])]});}
            var Q5;
            {var subQ5=sQuery(id+"F0.wireOp",EDGE,"E120");Q5=makeQuery(id+"F0.imprint","IMPRINT",FACE,{"disambiguationData":[TD([[makeQuery(id+"F0.imprint","IMPRINT",EDGE,{"derivedFrom":subQ5}),-1.0]])]});}
            var Q6;
            {var subQ5=sQuery(id+"F0.wireOp",EDGE,"E122");Q6=makeQuery(id+"F0.imprint","IMPRINT",FACE,{"disambiguationData":[TD([[makeQuery(id+"F0.imprint","IMPRINT",EDGE,{"derivedFrom":subQ5}),-1.0]])]});}
            var Q7;
            {var subQ5=sQuery(id+"F0.wireOp",EDGE,"E116");Q7=makeQuery(id+"F0.imprint","IMPRINT",FACE,{"disambiguationData":[TD([[makeQuery(id+"F0.imprint","IMPRINT",EDGE,{"derivedFrom":subQ5}),-1.0]])]});}
            var Q8;
            {var subQ5=sQuery(id+"F0.wireOp",EDGE,"E148.MirrorCS");Q8=makeQuery(id+"F0.imprint","IMPRINT",FACE,{"disambiguationData":[TD([[makeQuery(id+"F0.imprint","IMPRINT",EDGE,{"derivedFrom":subQ5}),1.0]])]});}
            var Q9;
            {var subQ5=sQuery(id+"F0.wireOp",EDGE,"E184");Q9=makeQuery(id+"F0.imprint","IMPRINT",FACE,{"disambiguationData":[TD([[makeQuery(id+"F0.imprint","IMPRINT",EDGE,{"derivedFrom":subQ5}),-1.0]])]});}
            var Q10;
            {var subQ5=sQuery(id+"F0.wireOp",EDGE,"E126");Q10=makeQuery(id+"F0.imprint","IMPRINT",FACE,{"disambiguationData":[TD([[makeQuery(id+"F0.imprint","IMPRINT",EDGE,{"derivedFrom":subQ5}),-1.0]])]});}
            var Q11;
            {var subQ5=sQuery(id+"F0.wireOp",EDGE,"E140.MirrorCS");Q11=makeQuery(id+"F0.imprint","IMPRINT",FACE,{"disambiguationData":[TD([[makeQuery(id+"F0.imprint","IMPRINT",EDGE,{"derivedFrom":subQ5}),1.0]])]});}
            var Q12;
            Q12=makeQuery(id+"F0.imprint","IMPRINT",FACE,{"disambiguationData":[TD([[makeQuery(id+"F0.imprint","IMPRINT",EDGE,{"derivedFrom":sQuery(id+"F0.wireOp",EDGE,"E3")}),-1.0]])]});
            var Q13;
            {var subQ5=sQuery(id+"F0.wireOp",EDGE,"E137.MirrorCS");Q13=makeQuery(id+"F0.imprint","IMPRINT",FACE,{"disambiguationData":[TD([[makeQuery(id+"F0.imprint","IMPRINT",EDGE,{"derivedFrom":subQ5}),1.0]])]});}
            var Q14;
            {var subQ5=sQuery(id+"F0.wireOp",EDGE,"E128");Q14=makeQuery(id+"F0.imprint","IMPRINT",FACE,{"disambiguationData":[TD([[makeQuery(id+"F0.imprint","IMPRINT",EDGE,{"derivedFrom":subQ5}),-1.0]])]});}
            var Q15;
            {var subQ5=sQuery(id+"F0.wireOp",EDGE,"E134.MirrorCS");Q15=makeQuery(id+"F0.imprint","IMPRINT",FACE,{"disambiguationData":[TD([[makeQuery(id+"F0.imprint","IMPRINT",EDGE,{"derivedFrom":subQ5}),1.0]])]});}
            var Q16;
            {var subQ5=sQuery(id+"F0.wireOp",EDGE,"E136.MirrorCS");Q16=makeQuery(id+"F0.imprint","IMPRINT",FACE,{"disambiguationData":[TD([[makeQuery(id+"F0.imprint","IMPRINT",EDGE,{"derivedFrom":subQ5}),1.0]])]});}
            var Q17;
            {var subQ5=sQuery(id+"F0.wireOp",EDGE,"E112");Q17=makeQuery(id+"F0.imprint","IMPRINT",FACE,{"disambiguationData":[TD([[makeQuery(id+"F0.imprint","IMPRINT",EDGE,{"derivedFrom":subQ5}),-1.0]])]});}
            var Q18;
            {var subQ5=sQuery(id+"F0.wireOp",EDGE,"E110");Q18=makeQuery(id+"F0.imprint","IMPRINT",FACE,{"disambiguationData":[TD([[makeQuery(id+"F0.imprint","IMPRINT",EDGE,{"derivedFrom":subQ5}),-1.0]])]});}
            var Q19;
            {var subQ5=sQuery(id+"F0.wireOp",EDGE,"E130.MirrorCS");Q19=makeQuery(id+"F0.imprint","IMPRINT",FACE,{"disambiguationData":[TD([[makeQuery(id+"F0.imprint","IMPRINT",EDGE,{"derivedFrom":subQ5}),1.0]])]});}
            var Q20;
            {var subQ5=sQuery(id+"F0.wireOp",EDGE,"E143.MirrorCS");Q20=makeQuery(id+"F0.imprint","IMPRINT",FACE,{"disambiguationData":[TD([[makeQuery(id+"F0.imprint","IMPRINT",EDGE,{"derivedFrom":subQ5}),1.0]])]});}
            var Q21;
            {var subQ5=sQuery(id+"F0.wireOp",EDGE,"E132.MirrorCS");Q21=makeQuery(id+"F0.imprint","IMPRINT",FACE,{"disambiguationData":[TD([[makeQuery(id+"F0.imprint","IMPRINT",EDGE,{"derivedFrom":subQ5}),1.0]])]});}
            var Q22;
            {var subQ5=sQuery(id+"F0.wireOp",EDGE,"E141.MirrorCS");Q22=makeQuery(id+"F0.imprint","IMPRINT",FACE,{"disambiguationData":[TD([[makeQuery(id+"F0.imprint","IMPRINT",EDGE,{"derivedFrom":subQ5}),1.0]])]});}
            var Q23;
            {var subQ5=sQuery(id+"F0.wireOp",EDGE,"E171.MirrorCS");Q23=makeQuery(id+"F0.imprint","IMPRINT",FACE,{"disambiguationData":[TD([[makeQuery(id+"F0.imprint","IMPRINT",EDGE,{"derivedFrom":subQ5}),-1.0]])]});}
            var Q24;
            {var subQ5=sQuery(id+"F0.wireOp",EDGE,"E168.MirrorCS");Q24=makeQuery(id+"F0.imprint","IMPRINT",FACE,{"disambiguationData":[TD([[makeQuery(id+"F0.imprint","IMPRINT",EDGE,{"derivedFrom":subQ5}),-1.0]])]});}
            var Q25;
            {var subQ5=sQuery(id+"F0.wireOp",EDGE,"E169.MirrorCS");Q25=makeQuery(id+"F0.imprint","IMPRINT",FACE,{"disambiguationData":[TD([[makeQuery(id+"F0.imprint","IMPRINT",EDGE,{"derivedFrom":subQ5}),-1.0]])]});}
            var Q26;
            {var subQ5=sQuery(id+"F0.wireOp",EDGE,"E166.MirrorCS");Q26=makeQuery(id+"F0.imprint","IMPRINT",FACE,{"disambiguationData":[TD([[makeQuery(id+"F0.imprint","IMPRINT",EDGE,{"derivedFrom":subQ5}),-1.0]])]});}
            var Q27;
            {var subQ5=sQuery(id+"F0.wireOp",EDGE,"E188.MirrorCS");Q27=makeQuery(id+"F0.imprint","IMPRINT",FACE,{"disambiguationData":[TD([[makeQuery(id+"F0.imprint","IMPRINT",EDGE,{"derivedFrom":subQ5}),1.0]])]});}
            var Q28;
            {var subQ5=sQuery(id+"F0.wireOp",EDGE,"E174.MirrorCS");Q28=makeQuery(id+"F0.imprint","IMPRINT",FACE,{"disambiguationData":[TD([[makeQuery(id+"F0.imprint","IMPRINT",EDGE,{"derivedFrom":subQ5}),-1.0]])]});}
            var Q29;
            {var subQ5=sQuery(id+"F0.wireOp",EDGE,"E176.MirrorCS");Q29=makeQuery(id+"F0.imprint","IMPRINT",FACE,{"disambiguationData":[TD([[makeQuery(id+"F0.imprint","IMPRINT",EDGE,{"derivedFrom":subQ5}),-1.0]])]});}
            var Q30;
            {var subQ5=sQuery(id+"F0.wireOp",EDGE,"E185.MirrorCS");Q30=makeQuery(id+"F0.imprint","IMPRINT",FACE,{"disambiguationData":[TD([[makeQuery(id+"F0.imprint","IMPRINT",EDGE,{"derivedFrom":subQ5}),1.0]])]});}
            var Q31;
            {var subQ5=sQuery(id+"F0.wireOp",EDGE,"E179.MirrorCS");Q31=makeQuery(id+"F0.imprint","IMPRINT",FACE,{"disambiguationData":[TD([[makeQuery(id+"F0.imprint","IMPRINT",EDGE,{"derivedFrom":subQ5}),-1.0]])]});}
            var Q32;
            {var subQ5=sQuery(id+"F0.wireOp",EDGE,"E177.MirrorCS");Q32=makeQuery(id+"F0.imprint","IMPRINT",FACE,{"disambiguationData":[TD([[makeQuery(id+"F0.imprint","IMPRINT",EDGE,{"derivedFrom":subQ5}),-1.0]])]});}
            var Q33;
            {var subQ5=sQuery(id+"F0.wireOp",EDGE,"E158.MirrorCS");Q33=makeQuery(id+"F0.imprint","IMPRINT",FACE,{"disambiguationData":[TD([[makeQuery(id+"F0.imprint","IMPRINT",EDGE,{"derivedFrom":subQ5}),1.0]])]});}
            var Q34;
            {var subQ5=sQuery(id+"F0.wireOp",EDGE,"E149.MirrorCS");Q34=makeQuery(id+"F0.imprint","IMPRINT",FACE,{"disambiguationData":[TD([[makeQuery(id+"F0.imprint","IMPRINT",EDGE,{"derivedFrom":subQ5}),1.0]])]});}
            var Q35;
            {var subQ5=sQuery(id+"F0.wireOp",EDGE,"E160.MirrorCS");Q35=makeQuery(id+"F0.imprint","IMPRINT",FACE,{"disambiguationData":[TD([[makeQuery(id+"F0.imprint","IMPRINT",EDGE,{"derivedFrom":subQ5}),1.0]])]});}
            var Q36;
            {var subQ5=sQuery(id+"F0.wireOp",EDGE,"E152.MirrorCS");Q36=makeQuery(id+"F0.imprint","IMPRINT",FACE,{"disambiguationData":[TD([[makeQuery(id+"F0.imprint","IMPRINT",EDGE,{"derivedFrom":subQ5}),1.0]])]});}
            var Q37;
            {var subQ5=sQuery(id+"F0.wireOp",EDGE,"E155.MirrorCS");Q37=makeQuery(id+"F0.imprint","IMPRINT",FACE,{"disambiguationData":[TD([[makeQuery(id+"F0.imprint","IMPRINT",EDGE,{"derivedFrom":subQ5}),1.0]])]});}
            var Q38;
            {var subQ5=sQuery(id+"F0.wireOp",EDGE,"E163.MirrorCS");Q38=makeQuery(id+"F0.imprint","IMPRINT",FACE,{"disambiguationData":[TD([[makeQuery(id+"F0.imprint","IMPRINT",EDGE,{"derivedFrom":subQ5}),1.0]])]});}
            var Q39;
            {var subQ5=sQuery(id+"F0.wireOp",EDGE,"E153.MirrorCS");Q39=makeQuery(id+"F0.imprint","IMPRINT",FACE,{"disambiguationData":[TD([[makeQuery(id+"F0.imprint","IMPRINT",EDGE,{"derivedFrom":subQ5}),1.0]])]});}
            var Q40;
            {var subQ5=sQuery(id+"F0.wireOp",EDGE,"E161.MirrorCS");Q40=makeQuery(id+"F0.imprint","IMPRINT",FACE,{"disambiguationData":[TD([[makeQuery(id+"F0.imprint","IMPRINT",EDGE,{"derivedFrom":subQ5}),1.0]])]});}
            extrude(context, id + "F1", {"entities" : qUnion([Q0, Q1, Q2, Q3, Q4, Q5, Q6, Q7, Q8, Q9, Q10, Q11, Q12, Q13, Q14, Q15, Q16, Q17, Q18, Q19, Q20, Q21, Q22, Q23, Q24, Q25, Q26, Q27, Q28, Q29, Q30, Q31, Q32, Q33, Q34, Q35, Q36, Q37, Q38, Q39, Q40]), "depth" : 6.35 * mm});
        }
        {
            var Q0;
            Q0=makeQuery(id+"F0.imprint","IMPRINT",FACE,{"disambiguationData":[TD([[makeQuery(id+"F0.imprint","IMPRINT",EDGE,{"derivedFrom":sQuery(id+"F0.wireOp",EDGE,"E1")}),-1.0]])]});
            var Q1;
            {var subQ0=sQuery(id+"F0.wireOp",EDGE,"E39");var subQ1=sQuery(id+"F0.wireOp",EDGE,"E0");var subQ2=makeQuery(id+"F0.imprint","INTERSECT",VERTEX,{"derivedFrom":[subQ1,subQ0]});Q1=makeQuery(id+"F0.imprint","IMPRINT",FACE,{"disambiguationData":[TD([[makeQuery(id+"F0.imprint","IMPRINT",EDGE,{"disambiguationData":[TD([[subQ2,-1.0]])],"derivedFrom":subQ1}),1.0]])]});}
            var Q2;
            {var subQ0=sQuery(id+"F0.wireOp",EDGE,"E50");Q2=makeQuery(id+"F0.imprint","IMPRINT",FACE,{"disambiguationData":[TD([[makeQuery(id+"F0.imprint","IMPRINT",EDGE,{"derivedFrom":subQ0}),-1.0]])]});}
            var Q3;
            {var subQ0=sQuery(id+"F0.wireOp",EDGE,"E45");Q3=makeQuery(id+"F0.imprint","IMPRINT",FACE,{"disambiguationData":[TD([[makeQuery(id+"F0.imprint","IMPRINT",EDGE,{"derivedFrom":subQ0}),-1.0]])]});}
            var Q4;
            {var subQ0=sQuery(id+"F0.wireOp",EDGE,"E55");Q4=makeQuery(id+"F0.imprint","IMPRINT",FACE,{"disambiguationData":[TD([[makeQuery(id+"F0.imprint","IMPRINT",EDGE,{"derivedFrom":subQ0}),-1.0]])]});}
            var Q5;
            {var subQ0=sQuery(id+"F0.wireOp",EDGE,"E60");Q5=makeQuery(id+"F0.imprint","IMPRINT",FACE,{"disambiguationData":[TD([[makeQuery(id+"F0.imprint","IMPRINT",EDGE,{"derivedFrom":subQ0}),-1.0]])]});}
            var Q6;
            {var subQ0=sQuery(id+"F0.wireOp",EDGE,"E70.MirrorCS");Q6=makeQuery(id+"F0.imprint","IMPRINT",FACE,{"disambiguationData":[TD([[makeQuery(id+"F0.imprint","IMPRINT",EDGE,{"derivedFrom":subQ0}),1.0]])]});}
            var Q7;
            {var subQ0=sQuery(id+"F0.wireOp",EDGE,"E71.MirrorCS");var subQ1=sQuery(id+"F0.wireOp",EDGE,"E0");var subQ2=makeQuery(id+"F0.imprint","INTERSECT",VERTEX,{"derivedFrom":[subQ1,subQ0]});Q7=makeQuery(id+"F0.imprint","IMPRINT",FACE,{"disambiguationData":[TD([[makeQuery(id+"F0.imprint","IMPRINT",EDGE,{"disambiguationData":[TD([[subQ2,1.0]])],"derivedFrom":subQ1}),1.0]])]});}
            var Q8;
            {var subQ5=sQuery(id+"F0.wireOp",EDGE,"E65.MirrorCS");Q8=makeQuery(id+"F0.imprint","IMPRINT",FACE,{"disambiguationData":[TD([[makeQuery(id+"F0.imprint","IMPRINT",EDGE,{"derivedFrom":subQ5}),-1.0]])]});}
            var Q9;
            {var subQ5=sQuery(id+"F0.wireOp",EDGE,"E12.MirrorCS");Q9=makeQuery(id+"F0.imprint","IMPRINT",FACE,{"disambiguationData":[TD([[makeQuery(id+"F0.imprint","IMPRINT",EDGE,{"derivedFrom":subQ5}),-1.0]])]});}
            var Q10;
            {var subQ5=sQuery(id+"F0.wireOp",EDGE,"E91.MirrorCS");Q10=makeQuery(id+"F0.imprint","IMPRINT",FACE,{"disambiguationData":[TD([[makeQuery(id+"F0.imprint","IMPRINT",EDGE,{"derivedFrom":subQ5}),1.0]])]});}
            var Q11;
            {var subQ0=sQuery(id+"F0.wireOp",EDGE,"E8");Q11=makeQuery(id+"F0.imprint","IMPRINT",FACE,{"disambiguationData":[TD([[makeQuery(id+"F0.imprint","IMPRINT",EDGE,{"derivedFrom":subQ0}),1.0]])]});}
            var Q12;
            {var subQ5=sQuery(id+"F0.wireOp",EDGE,"E88.MirrorCS");Q12=makeQuery(id+"F0.imprint","IMPRINT",FACE,{"disambiguationData":[TD([[makeQuery(id+"F0.imprint","IMPRINT",EDGE,{"derivedFrom":subQ5}),-1.0]])]});}
            var Q13;
            {var subQ0=sQuery(id+"F0.wireOp",EDGE,"E9.MirrorCS");Q13=makeQuery(id+"F0.imprint","IMPRINT",FACE,{"disambiguationData":[TD([[makeQuery(id+"F0.imprint","IMPRINT",EDGE,{"derivedFrom":subQ0}),1.0]])]});}
            var Q14;
            {var subQ5=sQuery(id+"F0.wireOp",EDGE,"E83.MirrorCS");Q14=makeQuery(id+"F0.imprint","IMPRINT",FACE,{"disambiguationData":[TD([[makeQuery(id+"F0.imprint","IMPRINT",EDGE,{"derivedFrom":subQ5}),-1.0]])]});}
            var Q15;
            {var subQ0=sQuery(id+"F0.wireOp",EDGE,"E16");Q15=makeQuery(id+"F0.imprint","IMPRINT",FACE,{"disambiguationData":[TD([[makeQuery(id+"F0.imprint","IMPRINT",EDGE,{"derivedFrom":subQ0}),-1.0]])]});}
            var Q16;
            {var subQ5=sQuery(id+"F0.wireOp",EDGE,"E78.MirrorCS");Q16=makeQuery(id+"F0.imprint","IMPRINT",FACE,{"disambiguationData":[TD([[makeQuery(id+"F0.imprint","IMPRINT",EDGE,{"derivedFrom":subQ5}),-1.0]])]});}
            var Q17;
            {var subQ0=sQuery(id+"F0.wireOp",EDGE,"E21");Q17=makeQuery(id+"F0.imprint","IMPRINT",FACE,{"disambiguationData":[TD([[makeQuery(id+"F0.imprint","IMPRINT",EDGE,{"derivedFrom":subQ0}),-1.0]])]});}
            var Q18;
            {var subQ0=sQuery(id+"F0.wireOp",EDGE,"E26");Q18=makeQuery(id+"F0.imprint","IMPRINT",FACE,{"disambiguationData":[TD([[makeQuery(id+"F0.imprint","IMPRINT",EDGE,{"derivedFrom":subQ0}),-1.0]])]});}
            var Q19;
            {var subQ5=sQuery(id+"F0.wireOp",EDGE,"E76.MirrorCS");Q19=makeQuery(id+"F0.imprint","IMPRINT",FACE,{"disambiguationData":[TD([[makeQuery(id+"F0.imprint","IMPRINT",EDGE,{"derivedFrom":subQ5}),-1.0]])]});}
            var Q20;
            {var subQ5=sQuery(id+"F0.wireOp",EDGE,"E57");Q20=makeQuery(id+"F0.imprint","IMPRINT",FACE,{"disambiguationData":[TD([[makeQuery(id+"F0.imprint","IMPRINT",EDGE,{"derivedFrom":subQ5}),1.0]])]});}
            var Q21;
            {var subQ5=sQuery(id+"F0.wireOp",EDGE,"E47");Q21=makeQuery(id+"F0.imprint","IMPRINT",FACE,{"disambiguationData":[TD([[makeQuery(id+"F0.imprint","IMPRINT",EDGE,{"derivedFrom":subQ5}),1.0]])]});}
            var Q22;
            {var subQ5=sQuery(id+"F0.wireOp",EDGE,"E52");Q22=makeQuery(id+"F0.imprint","IMPRINT",FACE,{"disambiguationData":[TD([[makeQuery(id+"F0.imprint","IMPRINT",EDGE,{"derivedFrom":subQ5}),1.0]])]});}
            var Q23;
            {var subQ5=sQuery(id+"F0.wireOp",EDGE,"E68.MirrorCS");Q23=makeQuery(id+"F0.imprint","IMPRINT",FACE,{"disambiguationData":[TD([[makeQuery(id+"F0.imprint","IMPRINT",EDGE,{"derivedFrom":subQ5}),-1.0]])]});}
            var Q24;
            {var subQ5=sQuery(id+"F0.wireOp",EDGE,"E106.MirrorCS");Q24=makeQuery(id+"F0.imprint","IMPRINT",FACE,{"disambiguationData":[TD([[makeQuery(id+"F0.imprint","IMPRINT",EDGE,{"derivedFrom":subQ5}),-1.0]])]});}
            var Q25;
            {var subQ5=sQuery(id+"F0.wireOp",EDGE,"E102.MirrorCS");Q25=makeQuery(id+"F0.imprint","IMPRINT",FACE,{"disambiguationData":[TD([[makeQuery(id+"F0.imprint","IMPRINT",EDGE,{"derivedFrom":subQ5}),-1.0]])]});}
            var Q26;
            {var subQ5=sQuery(id+"F0.wireOp",EDGE,"E100.MirrorCS");Q26=makeQuery(id+"F0.imprint","IMPRINT",FACE,{"disambiguationData":[TD([[makeQuery(id+"F0.imprint","IMPRINT",EDGE,{"derivedFrom":subQ5}),-1.0]])]});}
            var Q27;
            {var subQ5=sQuery(id+"F0.wireOp",EDGE,"E95.MirrorCS");Q27=makeQuery(id+"F0.imprint","IMPRINT",FACE,{"disambiguationData":[TD([[makeQuery(id+"F0.imprint","IMPRINT",EDGE,{"derivedFrom":subQ5}),-1.0]])]});}
            var Q28;
            {var subQ5=sQuery(id+"F0.wireOp",EDGE,"E5");Q28=makeQuery(id+"F0.imprint","IMPRINT",FACE,{"disambiguationData":[TD([[makeQuery(id+"F0.imprint","IMPRINT",EDGE,{"derivedFrom":subQ5}),1.0]])]});}
            var Q29;
            {var subQ5=sQuery(id+"F0.wireOp",EDGE,"E13");Q29=makeQuery(id+"F0.imprint","IMPRINT",FACE,{"disambiguationData":[TD([[makeQuery(id+"F0.imprint","IMPRINT",EDGE,{"derivedFrom":subQ5}),1.0]])]});}
            var Q30;
            {var subQ5=sQuery(id+"F0.wireOp",EDGE,"E18");Q30=makeQuery(id+"F0.imprint","IMPRINT",FACE,{"disambiguationData":[TD([[makeQuery(id+"F0.imprint","IMPRINT",EDGE,{"derivedFrom":subQ5}),1.0]])]});}
            var Q31;
            {var subQ5=sQuery(id+"F0.wireOp",EDGE,"E23");Q31=makeQuery(id+"F0.imprint","IMPRINT",FACE,{"disambiguationData":[TD([[makeQuery(id+"F0.imprint","IMPRINT",EDGE,{"derivedFrom":subQ5}),1.0]])]});}
            var Q32;
            {var subQ5=sQuery(id+"F0.wireOp",EDGE,"E28");Q32=makeQuery(id+"F0.imprint","IMPRINT",FACE,{"disambiguationData":[TD([[makeQuery(id+"F0.imprint","IMPRINT",EDGE,{"derivedFrom":subQ5}),1.0]])]});}
            var Q33;
            {var subQ5=sQuery(id+"F0.wireOp",EDGE,"E33");Q33=makeQuery(id+"F0.imprint","IMPRINT",FACE,{"disambiguationData":[TD([[makeQuery(id+"F0.imprint","IMPRINT",EDGE,{"derivedFrom":subQ5}),1.0]])]});}
            var Q34;
            {var subQ5=sQuery(id+"F0.wireOp",EDGE,"E38");Q34=makeQuery(id+"F0.imprint","IMPRINT",FACE,{"disambiguationData":[TD([[makeQuery(id+"F0.imprint","IMPRINT",EDGE,{"derivedFrom":subQ5}),1.0]])]});}
            var Q35;
            {var subQ5=sQuery(id+"F0.wireOp",EDGE,"E42");Q35=makeQuery(id+"F0.imprint","IMPRINT",FACE,{"disambiguationData":[TD([[makeQuery(id+"F0.imprint","IMPRINT",EDGE,{"derivedFrom":subQ5}),1.0]])]});}
            var Q36;
            {var subQ5=sQuery(id+"F0.wireOp",EDGE,"E72.MirrorCS");Q36=makeQuery(id+"F0.imprint","IMPRINT",FACE,{"disambiguationData":[TD([[makeQuery(id+"F0.imprint","IMPRINT",EDGE,{"derivedFrom":subQ5}),-1.0]])]});}
            var Q37;
            {var subQ0=sQuery(id+"F0.wireOp",EDGE,"E31");Q37=makeQuery(id+"F0.imprint","IMPRINT",FACE,{"disambiguationData":[TD([[makeQuery(id+"F0.imprint","IMPRINT",EDGE,{"derivedFrom":subQ0}),-1.0]])]});}
            var Q38;
            {var subQ0=sQuery(id+"F0.wireOp",EDGE,"E36");Q38=makeQuery(id+"F0.imprint","IMPRINT",FACE,{"disambiguationData":[TD([[makeQuery(id+"F0.imprint","IMPRINT",EDGE,{"derivedFrom":subQ0}),-1.0]])]});}
            var Q39;
            {var subQ0=sQuery(id+"F0.wireOp",EDGE,"E41");Q39=makeQuery(id+"F0.imprint","IMPRINT",FACE,{"disambiguationData":[TD([[makeQuery(id+"F0.imprint","IMPRINT",EDGE,{"derivedFrom":subQ0}),-1.0]])]});}
            var Q40;
            {var subQ0=sQuery(id+"F0.wireOp",EDGE,"E82.MirrorCS");var subQ1=sQuery(id+"F0.wireOp",EDGE,"E0");var subQ2=makeQuery(id+"F0.imprint","INTERSECT",VERTEX,{"derivedFrom":[subQ1,subQ0]});Q40=makeQuery(id+"F0.imprint","IMPRINT",FACE,{"disambiguationData":[TD([[makeQuery(id+"F0.imprint","IMPRINT",EDGE,{"disambiguationData":[TD([[subQ2,-1.0]])],"derivedFrom":subQ1}),1.0]])]});}
            var Q41;
            {var subQ0=sQuery(id+"F0.wireOp",EDGE,"E7");var subQ1=sQuery(id+"F0.wireOp",EDGE,"E0");var subQ2=makeQuery(id+"F0.imprint","INTERSECT",VERTEX,{"derivedFrom":[subQ1,subQ0]});Q41=makeQuery(id+"F0.imprint","IMPRINT",FACE,{"disambiguationData":[TD([[makeQuery(id+"F0.imprint","IMPRINT",EDGE,{"disambiguationData":[TD([[subQ2,-1.0]])],"derivedFrom":subQ1}),1.0]])]});}
            var Q42;
            {var subQ0=sQuery(id+"F0.wireOp",EDGE,"e1ac4ada-cdff-4511-8510-e6a0fec7607d0.MirrorCS");var subQ1=sQuery(id+"F0.wireOp",EDGE,"E0");var subQ2=makeQuery(id+"F0.imprint","INTERSECT",VERTEX,{"derivedFrom":[subQ1,subQ0]});Q42=makeQuery(id+"F0.imprint","IMPRINT",FACE,{"disambiguationData":[TD([[makeQuery(id+"F0.imprint","IMPRINT",EDGE,{"disambiguationData":[TD([[subQ2,-1.0]])],"derivedFrom":subQ1}),1.0]])]});}
            var Q43;
            {var subQ0=sQuery(id+"F0.wireOp",EDGE,"E30");var subQ1=sQuery(id+"F0.wireOp",EDGE,"E0");var subQ2=makeQuery(id+"F0.imprint","INTERSECT",VERTEX,{"derivedFrom":[subQ1,subQ0]});Q43=makeQuery(id+"F0.imprint","IMPRINT",FACE,{"disambiguationData":[TD([[makeQuery(id+"F0.imprint","IMPRINT",EDGE,{"disambiguationData":[TD([[subQ2,-1.0]])],"derivedFrom":subQ1}),1.0]])]});}
            var Q44;
            {var subQ0=sQuery(id+"F0.wireOp",EDGE,"E105.MirrorCS");var subQ1=sQuery(id+"F0.wireOp",EDGE,"E0");var subQ2=makeQuery(id+"F0.imprint","INTERSECT",VERTEX,{"derivedFrom":[subQ1,subQ0]});Q44=makeQuery(id+"F0.imprint","IMPRINT",FACE,{"disambiguationData":[TD([[makeQuery(id+"F0.imprint","IMPRINT",EDGE,{"disambiguationData":[TD([[subQ2,-1.0]])],"derivedFrom":subQ1}),1.0]])]});}
            var Q45;
            {var subQ0=sQuery(id+"F0.wireOp",EDGE,"E35");var subQ1=sQuery(id+"F0.wireOp",EDGE,"E0");var subQ2=makeQuery(id+"F0.imprint","INTERSECT",VERTEX,{"derivedFrom":[subQ1,subQ0]});Q45=makeQuery(id+"F0.imprint","IMPRINT",FACE,{"disambiguationData":[TD([[makeQuery(id+"F0.imprint","IMPRINT",EDGE,{"disambiguationData":[TD([[subQ2,-1.0]])],"derivedFrom":subQ1}),1.0]])]});}
            var Q46;
            {var subQ0=sQuery(id+"F0.wireOp",EDGE,"E11.MirrorCS");var subQ1=sQuery(id+"F0.wireOp",EDGE,"E0");var subQ2=makeQuery(id+"F0.imprint","INTERSECT",VERTEX,{"derivedFrom":[subQ1,subQ0]});Q46=makeQuery(id+"F0.imprint","IMPRINT",FACE,{"disambiguationData":[TD([[makeQuery(id+"F0.imprint","IMPRINT",EDGE,{"disambiguationData":[TD([[subQ2,-1.0]])],"derivedFrom":subQ1}),1.0]])]});}
            var Q47;
            {var subQ0=sQuery(id+"F0.wireOp",EDGE,"E59");var subQ1=sQuery(id+"F0.wireOp",EDGE,"E0");var subQ2=makeQuery(id+"F0.imprint","INTERSECT",VERTEX,{"derivedFrom":[subQ1,subQ0]});Q47=makeQuery(id+"F0.imprint","IMPRINT",FACE,{"disambiguationData":[TD([[makeQuery(id+"F0.imprint","IMPRINT",EDGE,{"disambiguationData":[TD([[subQ2,-1.0]])],"derivedFrom":subQ1}),1.0]])]});}
            var Q48;
            {var subQ0=sQuery(id+"F0.wireOp",EDGE,"E64.MirrorCS");var subQ1=sQuery(id+"F0.wireOp",EDGE,"E0");var subQ2=makeQuery(id+"F0.imprint","INTERSECT",VERTEX,{"derivedFrom":[subQ1,subQ0]});Q48=makeQuery(id+"F0.imprint","IMPRINT",FACE,{"disambiguationData":[TD([[makeQuery(id+"F0.imprint","IMPRINT",EDGE,{"disambiguationData":[TD([[subQ2,-1.0]])],"derivedFrom":subQ1}),1.0]])]});}
            var Q49;
            Q49=makeQuery(id+"F0.imprint","IMPRINT",FACE,{"disambiguationData":[TD([[makeQuery(id+"F0.imprint","IMPRINT",EDGE,{"derivedFrom":sQuery(id+"F0.wireOp",EDGE,"E1")}),1.0]])]});
            var Q50;
            {var subQ0=sQuery(id+"F0.wireOp",EDGE,"E43");var subQ1=sQuery(id+"F0.wireOp",EDGE,"E0");var subQ2=makeQuery(id+"F0.imprint","INTERSECT",VERTEX,{"derivedFrom":[subQ1,subQ0]});Q50=makeQuery(id+"F0.imprint","IMPRINT",FACE,{"disambiguationData":[TD([[makeQuery(id+"F0.imprint","IMPRINT",EDGE,{"disambiguationData":[TD([[subQ2,-1.0]])],"derivedFrom":subQ1}),1.0]])]});}
            var Q51;
            {var subQ0=sQuery(id+"F0.wireOp",EDGE,"E79.MirrorCS");var subQ1=sQuery(id+"F0.wireOp",EDGE,"E0");var subQ2=makeQuery(id+"F0.imprint","INTERSECT",VERTEX,{"derivedFrom":[subQ1,subQ0]});Q51=makeQuery(id+"F0.imprint","IMPRINT",FACE,{"disambiguationData":[TD([[makeQuery(id+"F0.imprint","IMPRINT",EDGE,{"disambiguationData":[TD([[subQ2,-1.0]])],"derivedFrom":subQ1}),1.0]])]});}
            var Q52;
            {var subQ0=sQuery(id+"F0.wireOp",EDGE,"E94.MirrorCS");var subQ1=sQuery(id+"F0.wireOp",EDGE,"E0");var subQ2=makeQuery(id+"F0.imprint","INTERSECT",VERTEX,{"derivedFrom":[subQ1,subQ0]});Q52=makeQuery(id+"F0.imprint","IMPRINT",FACE,{"disambiguationData":[TD([[makeQuery(id+"F0.imprint","IMPRINT",EDGE,{"disambiguationData":[TD([[subQ2,-1.0]])],"derivedFrom":subQ1}),1.0]])]});}
            var Q53;
            {var subQ0=sQuery(id+"F0.wireOp",EDGE,"E99.MirrorCS");var subQ1=sQuery(id+"F0.wireOp",EDGE,"E0");var subQ2=makeQuery(id+"F0.imprint","INTERSECT",VERTEX,{"derivedFrom":[subQ1,subQ0]});Q53=makeQuery(id+"F0.imprint","IMPRINT",FACE,{"disambiguationData":[TD([[makeQuery(id+"F0.imprint","IMPRINT",EDGE,{"disambiguationData":[TD([[subQ2,-1.0]])],"derivedFrom":subQ1}),1.0]])]});}
            var Q54;
            {var subQ0=sQuery(id+"F0.wireOp",EDGE,"E87.MirrorCS");var subQ1=sQuery(id+"F0.wireOp",EDGE,"E0");var subQ2=makeQuery(id+"F0.imprint","INTERSECT",VERTEX,{"derivedFrom":[subQ1,subQ0]});Q54=makeQuery(id+"F0.imprint","IMPRINT",FACE,{"disambiguationData":[TD([[makeQuery(id+"F0.imprint","IMPRINT",EDGE,{"disambiguationData":[TD([[subQ2,-1.0]])],"derivedFrom":subQ1}),1.0]])]});}
            var Q55;
            {var subQ0=sQuery(id+"F0.wireOp",EDGE,"E34");var subQ1=sQuery(id+"F0.wireOp",EDGE,"E0");var subQ2=makeQuery(id+"F0.imprint","INTERSECT",VERTEX,{"derivedFrom":[subQ1,subQ0]});Q55=makeQuery(id+"F0.imprint","IMPRINT",FACE,{"disambiguationData":[TD([[makeQuery(id+"F0.imprint","IMPRINT",EDGE,{"disambiguationData":[TD([[subQ2,-1.0]])],"derivedFrom":subQ1}),1.0]])]});}
            var Q56;
            {var subQ0=sQuery(id+"F0.wireOp",EDGE,"E58");var subQ1=sQuery(id+"F0.wireOp",EDGE,"E0");var subQ2=makeQuery(id+"F0.imprint","INTERSECT",VERTEX,{"derivedFrom":[subQ1,subQ0]});Q56=makeQuery(id+"F0.imprint","IMPRINT",FACE,{"disambiguationData":[TD([[makeQuery(id+"F0.imprint","IMPRINT",EDGE,{"disambiguationData":[TD([[subQ2,-1.0]])],"derivedFrom":subQ1}),1.0]])]});}
            var Q57;
            {var subQ0=sQuery(id+"F0.wireOp",EDGE,"E67.MirrorCS");var subQ1=sQuery(id+"F0.wireOp",EDGE,"E0");var subQ2=makeQuery(id+"F0.imprint","INTERSECT",VERTEX,{"derivedFrom":[subQ1,subQ0]});Q57=makeQuery(id+"F0.imprint","IMPRINT",FACE,{"disambiguationData":[TD([[makeQuery(id+"F0.imprint","IMPRINT",EDGE,{"disambiguationData":[TD([[subQ2,1.0]])],"derivedFrom":subQ1}),1.0]])]});}
            var Q58;
            {var subQ0=sQuery(id+"F0.wireOp",EDGE,"E25");var subQ1=sQuery(id+"F0.wireOp",EDGE,"E0");var subQ2=makeQuery(id+"F0.imprint","INTERSECT",VERTEX,{"derivedFrom":[subQ1,subQ0]});Q58=makeQuery(id+"F0.imprint","IMPRINT",FACE,{"disambiguationData":[TD([[makeQuery(id+"F0.imprint","IMPRINT",EDGE,{"disambiguationData":[TD([[subQ2,-1.0]])],"derivedFrom":subQ1}),1.0]])]});}
            var Q59;
            {var subQ0=sQuery(id+"F0.wireOp",EDGE,"E15");var subQ1=sQuery(id+"F0.wireOp",EDGE,"E0");var subQ2=makeQuery(id+"F0.imprint","INTERSECT",VERTEX,{"derivedFrom":[subQ1,subQ0]});Q59=makeQuery(id+"F0.imprint","IMPRINT",FACE,{"disambiguationData":[TD([[makeQuery(id+"F0.imprint","IMPRINT",EDGE,{"disambiguationData":[TD([[subQ2,-1.0]])],"derivedFrom":subQ1}),1.0]])]});}
            var Q60;
            {var subQ0=sQuery(id+"F0.wireOp",EDGE,"E48");var subQ1=sQuery(id+"F0.wireOp",EDGE,"E0");var subQ2=makeQuery(id+"F0.imprint","INTERSECT",VERTEX,{"derivedFrom":[subQ1,subQ0]});Q60=makeQuery(id+"F0.imprint","IMPRINT",FACE,{"disambiguationData":[TD([[makeQuery(id+"F0.imprint","IMPRINT",EDGE,{"disambiguationData":[TD([[subQ2,-1.0]])],"derivedFrom":subQ1}),1.0]])]});}
            var Q61;
            {var subQ0=sQuery(id+"F0.wireOp",EDGE,"E20");var subQ1=sQuery(id+"F0.wireOp",EDGE,"E0");var subQ2=makeQuery(id+"F0.imprint","INTERSECT",VERTEX,{"derivedFrom":[subQ1,subQ0]});Q61=makeQuery(id+"F0.imprint","IMPRINT",FACE,{"disambiguationData":[TD([[makeQuery(id+"F0.imprint","IMPRINT",EDGE,{"disambiguationData":[TD([[subQ2,-1.0]])],"derivedFrom":subQ1}),1.0]])]});}
            var Q62;
            {var subQ0=sQuery(id+"F0.wireOp",EDGE,"E53");var subQ1=sQuery(id+"F0.wireOp",EDGE,"E0");var subQ2=makeQuery(id+"F0.imprint","INTERSECT",VERTEX,{"derivedFrom":[subQ1,subQ0]});Q62=makeQuery(id+"F0.imprint","IMPRINT",FACE,{"disambiguationData":[TD([[makeQuery(id+"F0.imprint","IMPRINT",EDGE,{"disambiguationData":[TD([[subQ2,-1.0]])],"derivedFrom":subQ1}),1.0]])]});}
            var Q63;
            {var subQ0=sQuery(id+"F0.wireOp",EDGE,"E66.MirrorCS");var subQ1=sQuery(id+"F0.wireOp",EDGE,"E0");var subQ2=makeQuery(id+"F0.imprint","INTERSECT",VERTEX,{"derivedFrom":[subQ1,subQ0]});Q63=makeQuery(id+"F0.imprint","IMPRINT",FACE,{"disambiguationData":[TD([[makeQuery(id+"F0.imprint","IMPRINT",EDGE,{"disambiguationData":[TD([[subQ2,-1.0]])],"derivedFrom":subQ1}),1.0]])]});}
            var Q64;
            {var subQ0=sQuery(id+"F0.wireOp",EDGE,"E62.MirrorCS");var subQ1=sQuery(id+"F0.wireOp",EDGE,"E0");var subQ2=makeQuery(id+"F0.imprint","INTERSECT",VERTEX,{"derivedFrom":[subQ1,subQ0]});Q64=makeQuery(id+"F0.imprint","IMPRINT",FACE,{"disambiguationData":[TD([[makeQuery(id+"F0.imprint","IMPRINT",EDGE,{"disambiguationData":[TD([[subQ2,-1.0]])],"derivedFrom":subQ1}),1.0]])]});}
            var Q65;
            {var subQ0=sQuery(id+"F0.wireOp",EDGE,"E101.MirrorCS");var subQ1=sQuery(id+"F0.wireOp",EDGE,"E0");var subQ2=makeQuery(id+"F0.imprint","INTERSECT",VERTEX,{"derivedFrom":[subQ1,subQ0]});Q65=makeQuery(id+"F0.imprint","IMPRINT",FACE,{"disambiguationData":[TD([[makeQuery(id+"F0.imprint","IMPRINT",EDGE,{"disambiguationData":[TD([[subQ2,-1.0]])],"derivedFrom":subQ1}),1.0]])]});}
            var Q66;
            {var subQ0=sQuery(id+"F0.wireOp",EDGE,"E40");var subQ1=sQuery(id+"F0.wireOp",EDGE,"E0");var subQ2=makeQuery(id+"F0.imprint","INTERSECT",VERTEX,{"derivedFrom":[subQ1,subQ0]});Q66=makeQuery(id+"F0.imprint","IMPRINT",FACE,{"disambiguationData":[TD([[makeQuery(id+"F0.imprint","IMPRINT",EDGE,{"disambiguationData":[TD([[subQ2,-1.0]])],"derivedFrom":subQ1}),1.0]])]});}
            var Q67;
            {var subQ0=sQuery(id+"F0.wireOp",EDGE,"E89.MirrorCS");var subQ1=sQuery(id+"F0.wireOp",EDGE,"E0");var subQ2=makeQuery(id+"F0.imprint","INTERSECT",VERTEX,{"derivedFrom":[subQ1,subQ0]});Q67=makeQuery(id+"F0.imprint","IMPRINT",FACE,{"disambiguationData":[TD([[makeQuery(id+"F0.imprint","IMPRINT",EDGE,{"disambiguationData":[TD([[subQ2,-1.0]])],"derivedFrom":subQ1}),1.0]])]});}
            var Q68;
            {var subQ0=sQuery(id+"F0.wireOp",EDGE,"E98.MirrorCS");var subQ1=sQuery(id+"F0.wireOp",EDGE,"E0");var subQ2=makeQuery(id+"F0.imprint","INTERSECT",VERTEX,{"derivedFrom":[subQ1,subQ0]});Q68=makeQuery(id+"F0.imprint","IMPRINT",FACE,{"disambiguationData":[TD([[makeQuery(id+"F0.imprint","IMPRINT",EDGE,{"disambiguationData":[TD([[subQ2,-1.0]])],"derivedFrom":subQ1}),1.0]])]});}
            var Q69;
            {var subQ0=sQuery(id+"F0.wireOp",EDGE,"E44");var subQ1=sQuery(id+"F0.wireOp",EDGE,"E0");var subQ2=makeQuery(id+"F0.imprint","INTERSECT",VERTEX,{"derivedFrom":[subQ1,subQ0]});Q69=makeQuery(id+"F0.imprint","IMPRINT",FACE,{"disambiguationData":[TD([[makeQuery(id+"F0.imprint","IMPRINT",EDGE,{"disambiguationData":[TD([[subQ2,-1.0]])],"derivedFrom":subQ1}),1.0]])]});}
            var Q70;
            {var subQ0=sQuery(id+"F0.wireOp",EDGE,"E85.MirrorCS");var subQ1=sQuery(id+"F0.wireOp",EDGE,"E0");var subQ2=makeQuery(id+"F0.imprint","INTERSECT",VERTEX,{"derivedFrom":[subQ1,subQ0]});Q70=makeQuery(id+"F0.imprint","IMPRINT",FACE,{"disambiguationData":[TD([[makeQuery(id+"F0.imprint","IMPRINT",EDGE,{"disambiguationData":[TD([[subQ2,-1.0]])],"derivedFrom":subQ1}),1.0]])]});}
            var Q71;
            {var subQ0=sQuery(id+"F0.wireOp",EDGE,"E93.MirrorCS");var subQ1=sQuery(id+"F0.wireOp",EDGE,"E0");var subQ2=makeQuery(id+"F0.imprint","INTERSECT",VERTEX,{"derivedFrom":[subQ1,subQ0]});Q71=makeQuery(id+"F0.imprint","IMPRINT",FACE,{"disambiguationData":[TD([[makeQuery(id+"F0.imprint","IMPRINT",EDGE,{"disambiguationData":[TD([[subQ2,-1.0]])],"derivedFrom":subQ1}),1.0]])]});}
            var Q72;
            {var subQ0=sQuery(id+"F0.wireOp",EDGE,"E49");var subQ1=sQuery(id+"F0.wireOp",EDGE,"E0");var subQ2=makeQuery(id+"F0.imprint","INTERSECT",VERTEX,{"derivedFrom":[subQ1,subQ0]});Q72=makeQuery(id+"F0.imprint","IMPRINT",FACE,{"disambiguationData":[TD([[makeQuery(id+"F0.imprint","IMPRINT",EDGE,{"disambiguationData":[TD([[subQ2,-1.0]])],"derivedFrom":subQ1}),1.0]])]});}
            var Q73;
            {var subQ0=sQuery(id+"F0.wireOp",EDGE,"E84.MirrorCS");var subQ1=sQuery(id+"F0.wireOp",EDGE,"E0");var subQ2=makeQuery(id+"F0.imprint","INTERSECT",VERTEX,{"derivedFrom":[subQ1,subQ0]});Q73=makeQuery(id+"F0.imprint","IMPRINT",FACE,{"disambiguationData":[TD([[makeQuery(id+"F0.imprint","IMPRINT",EDGE,{"disambiguationData":[TD([[subQ2,-1.0]])],"derivedFrom":subQ1}),1.0]])]});}
            var Q74;
            {var subQ0=sQuery(id+"F0.wireOp",EDGE,"E6");var subQ1=sQuery(id+"F0.wireOp",EDGE,"E0");var subQ2=makeQuery(id+"F0.imprint","INTERSECT",VERTEX,{"derivedFrom":[subQ1,subQ0]});Q74=makeQuery(id+"F0.imprint","IMPRINT",FACE,{"disambiguationData":[TD([[makeQuery(id+"F0.imprint","IMPRINT",EDGE,{"disambiguationData":[TD([[subQ2,-1.0]])],"derivedFrom":subQ1}),1.0]])]});}
            var Q75;
            {var subQ0=sQuery(id+"F0.wireOp",EDGE,"E54");var subQ1=sQuery(id+"F0.wireOp",EDGE,"E0");var subQ2=makeQuery(id+"F0.imprint","INTERSECT",VERTEX,{"derivedFrom":[subQ1,subQ0]});Q75=makeQuery(id+"F0.imprint","IMPRINT",FACE,{"disambiguationData":[TD([[makeQuery(id+"F0.imprint","IMPRINT",EDGE,{"disambiguationData":[TD([[subQ2,-1.0]])],"derivedFrom":subQ1}),1.0]])]});}
            var Q76;
            {var subQ0=sQuery(id+"F0.wireOp",EDGE,"E77.MirrorCS");var subQ1=sQuery(id+"F0.wireOp",EDGE,"E0");var subQ2=makeQuery(id+"F0.imprint","INTERSECT",VERTEX,{"derivedFrom":[subQ1,subQ0]});Q76=makeQuery(id+"F0.imprint","IMPRINT",FACE,{"disambiguationData":[TD([[makeQuery(id+"F0.imprint","IMPRINT",EDGE,{"disambiguationData":[TD([[subQ2,-1.0]])],"derivedFrom":subQ1}),1.0]])]});}
            var Q77;
            {var subQ0=sQuery(id+"F0.wireOp",EDGE,"E75.MirrorCS");var subQ1=sQuery(id+"F0.wireOp",EDGE,"E0");var subQ2=makeQuery(id+"F0.imprint","INTERSECT",VERTEX,{"derivedFrom":[subQ1,subQ0]});Q77=makeQuery(id+"F0.imprint","IMPRINT",FACE,{"disambiguationData":[TD([[makeQuery(id+"F0.imprint","IMPRINT",EDGE,{"disambiguationData":[TD([[subQ2,-1.0]])],"derivedFrom":subQ1}),1.0]])]});}
            var Q78;
            {var subQ0=sQuery(id+"F0.wireOp",EDGE,"E14");var subQ1=sQuery(id+"F0.wireOp",EDGE,"E0");var subQ2=makeQuery(id+"F0.imprint","INTERSECT",VERTEX,{"derivedFrom":[subQ1,subQ0]});Q78=makeQuery(id+"F0.imprint","IMPRINT",FACE,{"disambiguationData":[TD([[makeQuery(id+"F0.imprint","IMPRINT",EDGE,{"disambiguationData":[TD([[subQ2,-1.0]])],"derivedFrom":subQ1}),1.0]])]});}
            var Q79;
            {var subQ0=sQuery(id+"F0.wireOp",EDGE,"E67.MirrorCS");var subQ1=sQuery(id+"F0.wireOp",EDGE,"E0");var subQ2=makeQuery(id+"F0.imprint","INTERSECT",VERTEX,{"derivedFrom":[subQ1,subQ0]});Q79=makeQuery(id+"F0.imprint","IMPRINT",FACE,{"disambiguationData":[TD([[makeQuery(id+"F0.imprint","IMPRINT",EDGE,{"disambiguationData":[TD([[subQ2,-1.0]])],"derivedFrom":subQ1}),1.0]])]});}
            var Q80;
            {var subQ0=sQuery(id+"F0.wireOp",EDGE,"E19");var subQ1=sQuery(id+"F0.wireOp",EDGE,"E0");var subQ2=makeQuery(id+"F0.imprint","INTERSECT",VERTEX,{"derivedFrom":[subQ1,subQ0]});Q80=makeQuery(id+"F0.imprint","IMPRINT",FACE,{"disambiguationData":[TD([[makeQuery(id+"F0.imprint","IMPRINT",EDGE,{"disambiguationData":[TD([[subQ2,-1.0]])],"derivedFrom":subQ1}),1.0]])]});}
            var Q81;
            {var subQ0=sQuery(id+"F0.wireOp",EDGE,"E10.MirrorCS");var subQ1=sQuery(id+"F0.wireOp",EDGE,"E0");var subQ2=makeQuery(id+"F0.imprint","INTERSECT",VERTEX,{"derivedFrom":[subQ1,subQ0]});Q81=makeQuery(id+"F0.imprint","IMPRINT",FACE,{"disambiguationData":[TD([[makeQuery(id+"F0.imprint","IMPRINT",EDGE,{"disambiguationData":[TD([[subQ2,-1.0]])],"derivedFrom":subQ1}),1.0]])]});}
            var Q82;
            {var subQ0=sQuery(id+"F0.wireOp",EDGE,"E107.MirrorCS");var subQ1=sQuery(id+"F0.wireOp",EDGE,"E0");var subQ2=makeQuery(id+"F0.imprint","INTERSECT",VERTEX,{"derivedFrom":[subQ1,subQ0]});Q82=makeQuery(id+"F0.imprint","IMPRINT",FACE,{"disambiguationData":[TD([[makeQuery(id+"F0.imprint","IMPRINT",EDGE,{"disambiguationData":[TD([[subQ2,-1.0]])],"derivedFrom":subQ1}),1.0]])]});}
            var Q83;
            {var subQ0=sQuery(id+"F0.wireOp",EDGE,"E24");var subQ1=sQuery(id+"F0.wireOp",EDGE,"E0");var subQ2=makeQuery(id+"F0.imprint","INTERSECT",VERTEX,{"derivedFrom":[subQ1,subQ0]});Q83=makeQuery(id+"F0.imprint","IMPRINT",FACE,{"disambiguationData":[TD([[makeQuery(id+"F0.imprint","IMPRINT",EDGE,{"disambiguationData":[TD([[subQ2,-1.0]])],"derivedFrom":subQ1}),1.0]])]});}
            var Q84;
            {var subQ0=sQuery(id+"F0.wireOp",EDGE,"E92.MirrorCS");var subQ1=sQuery(id+"F0.wireOp",EDGE,"E0");var subQ2=makeQuery(id+"F0.imprint","INTERSECT",VERTEX,{"derivedFrom":[subQ1,subQ0]});Q84=makeQuery(id+"F0.imprint","IMPRINT",FACE,{"disambiguationData":[TD([[makeQuery(id+"F0.imprint","IMPRINT",EDGE,{"disambiguationData":[TD([[subQ2,-1.0]])],"derivedFrom":subQ1}),1.0]])]});}
            var Q85;
            {var subQ0=sQuery(id+"F0.wireOp",EDGE,"E103.MirrorCS");var subQ1=sQuery(id+"F0.wireOp",EDGE,"E0");var subQ2=makeQuery(id+"F0.imprint","INTERSECT",VERTEX,{"derivedFrom":[subQ1,subQ0]});Q85=makeQuery(id+"F0.imprint","IMPRINT",FACE,{"disambiguationData":[TD([[makeQuery(id+"F0.imprint","IMPRINT",EDGE,{"disambiguationData":[TD([[subQ2,-1.0]])],"derivedFrom":subQ1}),1.0]])]});}
            var Q86;
            {var subQ0=sQuery(id+"F0.wireOp",EDGE,"E29");var subQ1=sQuery(id+"F0.wireOp",EDGE,"E0");var subQ2=makeQuery(id+"F0.imprint","INTERSECT",VERTEX,{"derivedFrom":[subQ1,subQ0]});Q86=makeQuery(id+"F0.imprint","IMPRINT",FACE,{"disambiguationData":[TD([[makeQuery(id+"F0.imprint","IMPRINT",EDGE,{"disambiguationData":[TD([[subQ2,-1.0]])],"derivedFrom":subQ1}),1.0]])]});}
            extrude(context, id + "F2", {"entities" : qUnion([Q0, Q1, Q2, Q3, Q4, Q5, Q6, Q7, Q8, Q9, Q10, Q11, Q12, Q13, Q14, Q15, Q16, Q17, Q18, Q19, Q20, Q21, Q22, Q23, Q24, Q25, Q26, Q27, Q28, Q29, Q30, Q31, Q32, Q33, Q34, Q35, Q36, Q37, Q38, Q39, Q40, Q41, Q42, Q43, Q44, Q45, Q46, Q47, Q48, Q49, Q50, Q51, Q52, Q53, Q54, Q55, Q56, Q57, Q58, Q59, Q60, Q61, Q62, Q63, Q64, Q65, Q66, Q67, Q68, Q69, Q70, Q71, Q72, Q73, Q74, Q75, Q76, Q77, Q78, Q79, Q80, Q81, Q82, Q83, Q84, Q85, Q86]), "depth" : 25.4 * mm});
        }
    });
